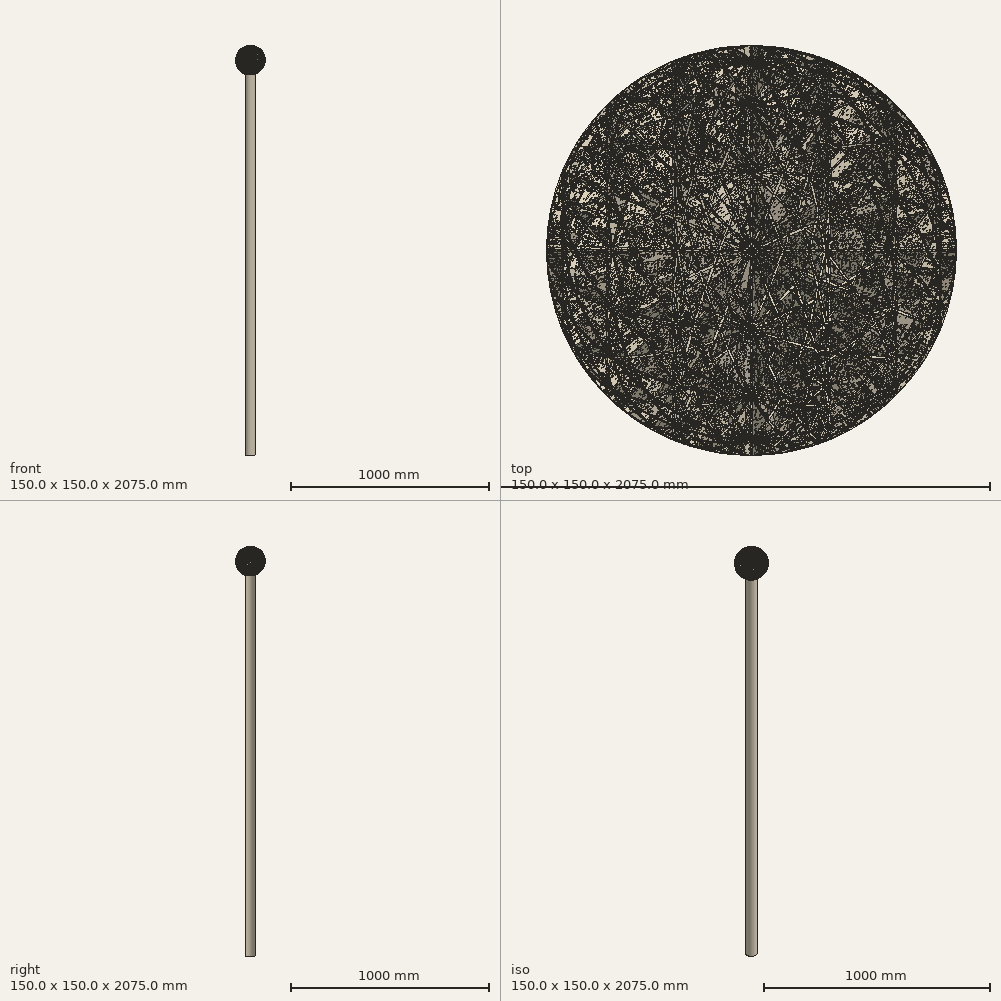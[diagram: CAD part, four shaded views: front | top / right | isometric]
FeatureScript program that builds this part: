
annotation { "Feature Type Name" : "Feature", "Feature Type Description" : "" }
export const myFeature = defineFeature(function(context is Context, id is Id, definition is map)
    precondition{}
    {
        {
            var Q0;
            Q0=qCreatedBy(makeId("Front.planeOp"),FACE);
            var sketch = newSketch(context, id + "F0", { "sketchPlane" : qUnion([Q0])});
            skCircle(sketch, "E0", {"center": v(0, 0) * mm, "radius": 75 * mm});
            skLineSegment(sketch, "E1", {"start": v(0, 0) * mm, "end": v(0, 98.01) * mm});
            skSolve(sketch);
        }
        {
            var Q0;
            Q0=qCreatedBy(makeId("Right.planeOp"),FACE);
            var sketch = newSketch(context, id + "F1", { "sketchPlane" : qUnion([Q0])});
            skCircle(sketch, "E2", {"center": v(0, 0) * mm, "radius": 75 * mm});
            skLineSegment(sketch, "E3", {"start": v(0, 0) * mm, "end": v(-91.52, 0) * mm});
            skSolve(sketch);
        }
        {
            var Q0;
            Q0=qCreatedBy(makeId("Top.planeOp"),FACE);
            var sketch = newSketch(context, id + "F2", { "sketchPlane" : qUnion([Q0])});
            skCircle(sketch, "E4", {"center": v(0, 0) * mm, "radius": 75 * mm});
            skLineSegment(sketch, "E5", {"start": v(0, 0) * mm, "end": v(107.76, 0) * mm});
            skSolve(sketch);
        }
        {
            var Q0;
            Q0=qCreatedBy(makeId("Top.planeOp"),FACE);
            var sketch = newSketch(context, id + "F3", { "sketchPlane" : qUnion([Q0])});
            skCircle(sketch, "E6", {"center": v(0, 0) * mm, "radius": 25 * mm});
            skSolve(sketch);
        }
        {
            var Q0;
            Q0=qSketchRegion(id+"F0",true);
            extrude(context, id + "F4", {"entities" : qUnion([Q0]), "endBound" : BoundingType.SYMMETRIC, "depth" : 1 * mm, "offsetDistance" : 25 * mm});
        }
        {
            var Q0;
            Q0=qSketchRegion(id+"F1",true);
            extrude(context, id + "F5", {"entities" : qUnion([Q0]), "operationType" : NewBodyOperationType.ADD, "endBound" : BoundingType.SYMMETRIC, "depth" : 1 * mm, "offsetDistance" : 25 * mm});
        }
        {
            var Q0;
            Q0=qSketchRegion(id+"F2",true);
            extrude(context, id + "F6", {"entities" : qUnion([Q0]), "operationType" : NewBodyOperationType.ADD, "endBound" : BoundingType.SYMMETRIC, "depth" : 1 * mm, "offsetDistance" : 25 * mm});
        }
        {
            var Q0;
            Q0 = qSketchRegion(id + "F3", true);
            extrude(context, id + "F7", {"entities" : qUnion([Q0]), "oppositeDirection" : true, "depth" : 2000 * mm, "offsetDistance" : 25 * mm});
        }
        {
            var Q0;
            Q0=makeQuery(id+"F4.opExtrude","SWEPT_BODY",BODY,{"disambiguationData":[OSD([sQuery(id+"F0.wireOp",EDGE,"E0")])]});
            var Q1;
            Q1=sQuery(id+"F0.wireOp",EDGE,"E1");
            var Q2;
            Q2=makeQuery(id+"F4.opExtrude","SWEPT_BODY",BODY,{"disambiguationData":[OSD([sQuery(id+"F0.wireOp",EDGE,"E0")])]});
            circularPattern(context, id + "F8", {"entities" : qUnion([Q0]), "axis" : qUnion([Q1]), "angle" : 360 * degree, "instanceCount" : 16, "equalSpace" : true});
        }
        {
            var Q0;
            Q0=makeQuery(id+"F4.opExtrude","SWEPT_BODY",BODY,{"disambiguationData":[OSD([sQuery(id+"F0.wireOp",EDGE,"E0")])]});
            var Q1;
            Q1=makeQuery(id+"F8.opPattern","COPY",BODY,{"derivedFrom":makeQuery(id+"F4.opExtrude","SWEPT_BODY",BODY,{"disambiguationData":[OSD([sQuery(id+"F0.wireOp",EDGE,"E0")])]}),"instanceName":"3"});
            var Q2;
            Q2=makeQuery(id+"F8.opPattern","COPY",BODY,{"derivedFrom":makeQuery(id+"F4.opExtrude","SWEPT_BODY",BODY,{"disambiguationData":[OSD([sQuery(id+"F0.wireOp",EDGE,"E0")])]}),"instanceName":"2"});
            var Q3;
            Q3=makeQuery(id+"F8.opPattern","COPY",BODY,{"derivedFrom":makeQuery(id+"F4.opExtrude","SWEPT_BODY",BODY,{"disambiguationData":[OSD([sQuery(id+"F0.wireOp",EDGE,"E0")])]}),"instanceName":"1"});
            var Q4;
            Q4=makeQuery(id+"F9.opPattern","COPY",BODY,{"derivedFrom":makeQuery(id+"F8.opPattern","COPY",BODY,{"derivedFrom":makeQuery(id+"F4.opExtrude","SWEPT_BODY",BODY,{"disambiguationData":[OSD([sQuery(id+"F0.wireOp",EDGE,"E0")])]}),"instanceName":"2"}),"instanceName":"1"});
            var Q5;
            Q5=makeQuery(id+"F9.opPattern","COPY",BODY,{"derivedFrom":makeQuery(id+"F8.opPattern","COPY",BODY,{"derivedFrom":makeQuery(id+"F4.opExtrude","SWEPT_BODY",BODY,{"disambiguationData":[OSD([sQuery(id+"F0.wireOp",EDGE,"E0")])]}),"instanceName":"1"}),"instanceName":"1"});
            var Q6;
            Q6=makeQuery(id+"F9.opPattern","COPY",BODY,{"derivedFrom":makeQuery(id+"F4.opExtrude","SWEPT_BODY",BODY,{"disambiguationData":[OSD([sQuery(id+"F0.wireOp",EDGE,"E0")])]}),"instanceName":"1"});
            var Q7;
            Q7=makeQuery(id+"F9.opPattern","COPY",BODY,{"derivedFrom":makeQuery(id+"F8.opPattern","COPY",BODY,{"derivedFrom":makeQuery(id+"F4.opExtrude","SWEPT_BODY",BODY,{"disambiguationData":[OSD([sQuery(id+"F0.wireOp",EDGE,"E0")])]}),"instanceName":"1"}),"instanceName":"8"});
            var Q8;
            Q8=makeQuery(id+"F9.opPattern","COPY",BODY,{"derivedFrom":makeQuery(id+"F8.opPattern","COPY",BODY,{"derivedFrom":makeQuery(id+"F4.opExtrude","SWEPT_BODY",BODY,{"disambiguationData":[OSD([sQuery(id+"F0.wireOp",EDGE,"E0")])]}),"instanceName":"15"}),"instanceName":"7"});
            var Q9;
            Q9=makeQuery(id+"F9.opPattern","COPY",BODY,{"derivedFrom":makeQuery(id+"F8.opPattern","COPY",BODY,{"derivedFrom":makeQuery(id+"F4.opExtrude","SWEPT_BODY",BODY,{"disambiguationData":[OSD([sQuery(id+"F0.wireOp",EDGE,"E0")])]}),"instanceName":"14"}),"instanceName":"7"});
            var Q10;
            Q10=makeQuery(id+"F9.opPattern","COPY",BODY,{"derivedFrom":makeQuery(id+"F8.opPattern","COPY",BODY,{"derivedFrom":makeQuery(id+"F4.opExtrude","SWEPT_BODY",BODY,{"disambiguationData":[OSD([sQuery(id+"F0.wireOp",EDGE,"E0")])]}),"instanceName":"13"}),"instanceName":"7"});
            var Q11;
            Q11=makeQuery(id+"F9.opPattern","COPY",BODY,{"derivedFrom":makeQuery(id+"F8.opPattern","COPY",BODY,{"derivedFrom":makeQuery(id+"F4.opExtrude","SWEPT_BODY",BODY,{"disambiguationData":[OSD([sQuery(id+"F0.wireOp",EDGE,"E0")])]}),"instanceName":"11"}),"instanceName":"7"});
            var Q12;
            Q12=makeQuery(id+"F9.opPattern","COPY",BODY,{"derivedFrom":makeQuery(id+"F8.opPattern","COPY",BODY,{"derivedFrom":makeQuery(id+"F4.opExtrude","SWEPT_BODY",BODY,{"disambiguationData":[OSD([sQuery(id+"F0.wireOp",EDGE,"E0")])]}),"instanceName":"10"}),"instanceName":"7"});
            var Q13;
            Q13=makeQuery(id+"F9.opPattern","COPY",BODY,{"derivedFrom":makeQuery(id+"F8.opPattern","COPY",BODY,{"derivedFrom":makeQuery(id+"F4.opExtrude","SWEPT_BODY",BODY,{"disambiguationData":[OSD([sQuery(id+"F0.wireOp",EDGE,"E0")])]}),"instanceName":"9"}),"instanceName":"7"});
            var Q14;
            Q14=makeQuery(id+"F9.opPattern","COPY",BODY,{"derivedFrom":makeQuery(id+"F8.opPattern","COPY",BODY,{"derivedFrom":makeQuery(id+"F4.opExtrude","SWEPT_BODY",BODY,{"disambiguationData":[OSD([sQuery(id+"F0.wireOp",EDGE,"E0")])]}),"instanceName":"7"}),"instanceName":"7"});
            var Q15;
            Q15=makeQuery(id+"F9.opPattern","COPY",BODY,{"derivedFrom":makeQuery(id+"F8.opPattern","COPY",BODY,{"derivedFrom":makeQuery(id+"F4.opExtrude","SWEPT_BODY",BODY,{"disambiguationData":[OSD([sQuery(id+"F0.wireOp",EDGE,"E0")])]}),"instanceName":"6"}),"instanceName":"7"});
            var Q16;
            Q16=makeQuery(id+"F9.opPattern","COPY",BODY,{"derivedFrom":makeQuery(id+"F8.opPattern","COPY",BODY,{"derivedFrom":makeQuery(id+"F4.opExtrude","SWEPT_BODY",BODY,{"disambiguationData":[OSD([sQuery(id+"F0.wireOp",EDGE,"E0")])]}),"instanceName":"5"}),"instanceName":"7"});
            var Q17;
            Q17=makeQuery(id+"F9.opPattern","COPY",BODY,{"derivedFrom":makeQuery(id+"F8.opPattern","COPY",BODY,{"derivedFrom":makeQuery(id+"F4.opExtrude","SWEPT_BODY",BODY,{"disambiguationData":[OSD([sQuery(id+"F0.wireOp",EDGE,"E0")])]}),"instanceName":"4"}),"instanceName":"7"});
            var Q18;
            Q18=makeQuery(id+"F9.opPattern","COPY",BODY,{"derivedFrom":makeQuery(id+"F8.opPattern","COPY",BODY,{"derivedFrom":makeQuery(id+"F4.opExtrude","SWEPT_BODY",BODY,{"disambiguationData":[OSD([sQuery(id+"F0.wireOp",EDGE,"E0")])]}),"instanceName":"3"}),"instanceName":"7"});
            var Q19;
            Q19=makeQuery(id+"F9.opPattern","COPY",BODY,{"derivedFrom":makeQuery(id+"F8.opPattern","COPY",BODY,{"derivedFrom":makeQuery(id+"F4.opExtrude","SWEPT_BODY",BODY,{"disambiguationData":[OSD([sQuery(id+"F0.wireOp",EDGE,"E0")])]}),"instanceName":"2"}),"instanceName":"7"});
            var Q20;
            Q20=makeQuery(id+"F9.opPattern","COPY",BODY,{"derivedFrom":makeQuery(id+"F8.opPattern","COPY",BODY,{"derivedFrom":makeQuery(id+"F4.opExtrude","SWEPT_BODY",BODY,{"disambiguationData":[OSD([sQuery(id+"F0.wireOp",EDGE,"E0")])]}),"instanceName":"1"}),"instanceName":"7"});
            var Q21;
            Q21=makeQuery(id+"F9.opPattern","COPY",BODY,{"derivedFrom":makeQuery(id+"F8.opPattern","COPY",BODY,{"derivedFrom":makeQuery(id+"F4.opExtrude","SWEPT_BODY",BODY,{"disambiguationData":[OSD([sQuery(id+"F0.wireOp",EDGE,"E0")])]}),"instanceName":"15"}),"instanceName":"6"});
            var Q22;
            Q22=makeQuery(id+"F9.opPattern","COPY",BODY,{"derivedFrom":makeQuery(id+"F8.opPattern","COPY",BODY,{"derivedFrom":makeQuery(id+"F4.opExtrude","SWEPT_BODY",BODY,{"disambiguationData":[OSD([sQuery(id+"F0.wireOp",EDGE,"E0")])]}),"instanceName":"13"}),"instanceName":"6"});
            var Q23;
            Q23=makeQuery(id+"F9.opPattern","COPY",BODY,{"derivedFrom":makeQuery(id+"F8.opPattern","COPY",BODY,{"derivedFrom":makeQuery(id+"F4.opExtrude","SWEPT_BODY",BODY,{"disambiguationData":[OSD([sQuery(id+"F0.wireOp",EDGE,"E0")])]}),"instanceName":"11"}),"instanceName":"6"});
            var Q24;
            Q24=makeQuery(id+"F9.opPattern","COPY",BODY,{"derivedFrom":makeQuery(id+"F8.opPattern","COPY",BODY,{"derivedFrom":makeQuery(id+"F4.opExtrude","SWEPT_BODY",BODY,{"disambiguationData":[OSD([sQuery(id+"F0.wireOp",EDGE,"E0")])]}),"instanceName":"10"}),"instanceName":"6"});
            var Q25;
            Q25=makeQuery(id+"F9.opPattern","COPY",BODY,{"derivedFrom":makeQuery(id+"F8.opPattern","COPY",BODY,{"derivedFrom":makeQuery(id+"F4.opExtrude","SWEPT_BODY",BODY,{"disambiguationData":[OSD([sQuery(id+"F0.wireOp",EDGE,"E0")])]}),"instanceName":"9"}),"instanceName":"6"});
            var Q26;
            Q26=makeQuery(id+"F9.opPattern","COPY",BODY,{"derivedFrom":makeQuery(id+"F8.opPattern","COPY",BODY,{"derivedFrom":makeQuery(id+"F4.opExtrude","SWEPT_BODY",BODY,{"disambiguationData":[OSD([sQuery(id+"F0.wireOp",EDGE,"E0")])]}),"instanceName":"7"}),"instanceName":"6"});
            var Q27;
            Q27=makeQuery(id+"F9.opPattern","COPY",BODY,{"derivedFrom":makeQuery(id+"F8.opPattern","COPY",BODY,{"derivedFrom":makeQuery(id+"F4.opExtrude","SWEPT_BODY",BODY,{"disambiguationData":[OSD([sQuery(id+"F0.wireOp",EDGE,"E0")])]}),"instanceName":"6"}),"instanceName":"6"});
            var Q28;
            Q28=makeQuery(id+"F9.opPattern","COPY",BODY,{"derivedFrom":makeQuery(id+"F8.opPattern","COPY",BODY,{"derivedFrom":makeQuery(id+"F4.opExtrude","SWEPT_BODY",BODY,{"disambiguationData":[OSD([sQuery(id+"F0.wireOp",EDGE,"E0")])]}),"instanceName":"5"}),"instanceName":"6"});
            var Q29;
            Q29=makeQuery(id+"F9.opPattern","COPY",BODY,{"derivedFrom":makeQuery(id+"F8.opPattern","COPY",BODY,{"derivedFrom":makeQuery(id+"F4.opExtrude","SWEPT_BODY",BODY,{"disambiguationData":[OSD([sQuery(id+"F0.wireOp",EDGE,"E0")])]}),"instanceName":"3"}),"instanceName":"6"});
            var Q30;
            Q30=makeQuery(id+"F9.opPattern","COPY",BODY,{"derivedFrom":makeQuery(id+"F8.opPattern","COPY",BODY,{"derivedFrom":makeQuery(id+"F4.opExtrude","SWEPT_BODY",BODY,{"disambiguationData":[OSD([sQuery(id+"F0.wireOp",EDGE,"E0")])]}),"instanceName":"2"}),"instanceName":"6"});
            var Q31;
            Q31=makeQuery(id+"F9.opPattern","COPY",BODY,{"derivedFrom":makeQuery(id+"F8.opPattern","COPY",BODY,{"derivedFrom":makeQuery(id+"F4.opExtrude","SWEPT_BODY",BODY,{"disambiguationData":[OSD([sQuery(id+"F0.wireOp",EDGE,"E0")])]}),"instanceName":"1"}),"instanceName":"6"});
            var Q32;
            Q32=makeQuery(id+"F9.opPattern","COPY",BODY,{"derivedFrom":makeQuery(id+"F4.opExtrude","SWEPT_BODY",BODY,{"disambiguationData":[OSD([sQuery(id+"F0.wireOp",EDGE,"E0")])]}),"instanceName":"6"});
            var Q33;
            Q33=makeQuery(id+"F9.opPattern","COPY",BODY,{"derivedFrom":makeQuery(id+"F8.opPattern","COPY",BODY,{"derivedFrom":makeQuery(id+"F4.opExtrude","SWEPT_BODY",BODY,{"disambiguationData":[OSD([sQuery(id+"F0.wireOp",EDGE,"E0")])]}),"instanceName":"14"}),"instanceName":"5"});
            var Q34;
            Q34=makeQuery(id+"F9.opPattern","COPY",BODY,{"derivedFrom":makeQuery(id+"F8.opPattern","COPY",BODY,{"derivedFrom":makeQuery(id+"F4.opExtrude","SWEPT_BODY",BODY,{"disambiguationData":[OSD([sQuery(id+"F0.wireOp",EDGE,"E0")])]}),"instanceName":"13"}),"instanceName":"5"});
            var Q35;
            Q35=makeQuery(id+"F9.opPattern","COPY",BODY,{"derivedFrom":makeQuery(id+"F8.opPattern","COPY",BODY,{"derivedFrom":makeQuery(id+"F4.opExtrude","SWEPT_BODY",BODY,{"disambiguationData":[OSD([sQuery(id+"F0.wireOp",EDGE,"E0")])]}),"instanceName":"11"}),"instanceName":"5"});
            var Q36;
            Q36=makeQuery(id+"F9.opPattern","COPY",BODY,{"derivedFrom":makeQuery(id+"F8.opPattern","COPY",BODY,{"derivedFrom":makeQuery(id+"F4.opExtrude","SWEPT_BODY",BODY,{"disambiguationData":[OSD([sQuery(id+"F0.wireOp",EDGE,"E0")])]}),"instanceName":"10"}),"instanceName":"5"});
            var Q37;
            Q37=makeQuery(id+"F9.opPattern","COPY",BODY,{"derivedFrom":makeQuery(id+"F8.opPattern","COPY",BODY,{"derivedFrom":makeQuery(id+"F4.opExtrude","SWEPT_BODY",BODY,{"disambiguationData":[OSD([sQuery(id+"F0.wireOp",EDGE,"E0")])]}),"instanceName":"9"}),"instanceName":"5"});
            var Q38;
            Q38=makeQuery(id+"F9.opPattern","COPY",BODY,{"derivedFrom":makeQuery(id+"F8.opPattern","COPY",BODY,{"derivedFrom":makeQuery(id+"F4.opExtrude","SWEPT_BODY",BODY,{"disambiguationData":[OSD([sQuery(id+"F0.wireOp",EDGE,"E0")])]}),"instanceName":"8"}),"instanceName":"5"});
            var Q39;
            Q39=makeQuery(id+"F9.opPattern","COPY",BODY,{"derivedFrom":makeQuery(id+"F8.opPattern","COPY",BODY,{"derivedFrom":makeQuery(id+"F4.opExtrude","SWEPT_BODY",BODY,{"disambiguationData":[OSD([sQuery(id+"F0.wireOp",EDGE,"E0")])]}),"instanceName":"7"}),"instanceName":"5"});
            var Q40;
            Q40=makeQuery(id+"F9.opPattern","COPY",BODY,{"derivedFrom":makeQuery(id+"F8.opPattern","COPY",BODY,{"derivedFrom":makeQuery(id+"F4.opExtrude","SWEPT_BODY",BODY,{"disambiguationData":[OSD([sQuery(id+"F0.wireOp",EDGE,"E0")])]}),"instanceName":"6"}),"instanceName":"5"});
            var Q41;
            Q41=makeQuery(id+"F9.opPattern","COPY",BODY,{"derivedFrom":makeQuery(id+"F8.opPattern","COPY",BODY,{"derivedFrom":makeQuery(id+"F4.opExtrude","SWEPT_BODY",BODY,{"disambiguationData":[OSD([sQuery(id+"F0.wireOp",EDGE,"E0")])]}),"instanceName":"5"}),"instanceName":"5"});
            var Q42;
            Q42=makeQuery(id+"F9.opPattern","COPY",BODY,{"derivedFrom":makeQuery(id+"F8.opPattern","COPY",BODY,{"derivedFrom":makeQuery(id+"F4.opExtrude","SWEPT_BODY",BODY,{"disambiguationData":[OSD([sQuery(id+"F0.wireOp",EDGE,"E0")])]}),"instanceName":"3"}),"instanceName":"5"});
            var Q43;
            Q43=makeQuery(id+"F9.opPattern","COPY",BODY,{"derivedFrom":makeQuery(id+"F8.opPattern","COPY",BODY,{"derivedFrom":makeQuery(id+"F4.opExtrude","SWEPT_BODY",BODY,{"disambiguationData":[OSD([sQuery(id+"F0.wireOp",EDGE,"E0")])]}),"instanceName":"2"}),"instanceName":"5"});
            var Q44;
            Q44=makeQuery(id+"F9.opPattern","COPY",BODY,{"derivedFrom":makeQuery(id+"F8.opPattern","COPY",BODY,{"derivedFrom":makeQuery(id+"F4.opExtrude","SWEPT_BODY",BODY,{"disambiguationData":[OSD([sQuery(id+"F0.wireOp",EDGE,"E0")])]}),"instanceName":"1"}),"instanceName":"5"});
            var Q45;
            Q45=makeQuery(id+"F9.opPattern","COPY",BODY,{"derivedFrom":makeQuery(id+"F4.opExtrude","SWEPT_BODY",BODY,{"disambiguationData":[OSD([sQuery(id+"F0.wireOp",EDGE,"E0")])]}),"instanceName":"5"});
            var Q46;
            Q46=makeQuery(id+"F9.opPattern","COPY",BODY,{"derivedFrom":makeQuery(id+"F8.opPattern","COPY",BODY,{"derivedFrom":makeQuery(id+"F4.opExtrude","SWEPT_BODY",BODY,{"disambiguationData":[OSD([sQuery(id+"F0.wireOp",EDGE,"E0")])]}),"instanceName":"13"}),"instanceName":"4"});
            var Q47;
            Q47=makeQuery(id+"F9.opPattern","COPY",BODY,{"derivedFrom":makeQuery(id+"F8.opPattern","COPY",BODY,{"derivedFrom":makeQuery(id+"F4.opExtrude","SWEPT_BODY",BODY,{"disambiguationData":[OSD([sQuery(id+"F0.wireOp",EDGE,"E0")])]}),"instanceName":"11"}),"instanceName":"4"});
            var Q48;
            Q48=makeQuery(id+"F9.opPattern","COPY",BODY,{"derivedFrom":makeQuery(id+"F8.opPattern","COPY",BODY,{"derivedFrom":makeQuery(id+"F4.opExtrude","SWEPT_BODY",BODY,{"disambiguationData":[OSD([sQuery(id+"F0.wireOp",EDGE,"E0")])]}),"instanceName":"10"}),"instanceName":"4"});
            var Q49;
            Q49=makeQuery(id+"F9.opPattern","COPY",BODY,{"derivedFrom":makeQuery(id+"F8.opPattern","COPY",BODY,{"derivedFrom":makeQuery(id+"F4.opExtrude","SWEPT_BODY",BODY,{"disambiguationData":[OSD([sQuery(id+"F0.wireOp",EDGE,"E0")])]}),"instanceName":"9"}),"instanceName":"4"});
            var Q50;
            Q50=makeQuery(id+"F9.opPattern","COPY",BODY,{"derivedFrom":makeQuery(id+"F8.opPattern","COPY",BODY,{"derivedFrom":makeQuery(id+"F4.opExtrude","SWEPT_BODY",BODY,{"disambiguationData":[OSD([sQuery(id+"F0.wireOp",EDGE,"E0")])]}),"instanceName":"7"}),"instanceName":"4"});
            var Q51;
            Q51=makeQuery(id+"F9.opPattern","COPY",BODY,{"derivedFrom":makeQuery(id+"F8.opPattern","COPY",BODY,{"derivedFrom":makeQuery(id+"F4.opExtrude","SWEPT_BODY",BODY,{"disambiguationData":[OSD([sQuery(id+"F0.wireOp",EDGE,"E0")])]}),"instanceName":"6"}),"instanceName":"4"});
            var Q52;
            Q52=makeQuery(id+"F9.opPattern","COPY",BODY,{"derivedFrom":makeQuery(id+"F8.opPattern","COPY",BODY,{"derivedFrom":makeQuery(id+"F4.opExtrude","SWEPT_BODY",BODY,{"disambiguationData":[OSD([sQuery(id+"F0.wireOp",EDGE,"E0")])]}),"instanceName":"5"}),"instanceName":"4"});
            var Q53;
            Q53=makeQuery(id+"F9.opPattern","COPY",BODY,{"derivedFrom":makeQuery(id+"F8.opPattern","COPY",BODY,{"derivedFrom":makeQuery(id+"F4.opExtrude","SWEPT_BODY",BODY,{"disambiguationData":[OSD([sQuery(id+"F0.wireOp",EDGE,"E0")])]}),"instanceName":"3"}),"instanceName":"4"});
            var Q54;
            Q54=makeQuery(id+"F9.opPattern","COPY",BODY,{"derivedFrom":makeQuery(id+"F8.opPattern","COPY",BODY,{"derivedFrom":makeQuery(id+"F4.opExtrude","SWEPT_BODY",BODY,{"disambiguationData":[OSD([sQuery(id+"F0.wireOp",EDGE,"E0")])]}),"instanceName":"2"}),"instanceName":"4"});
            var Q55;
            Q55=makeQuery(id+"F9.opPattern","COPY",BODY,{"derivedFrom":makeQuery(id+"F8.opPattern","COPY",BODY,{"derivedFrom":makeQuery(id+"F4.opExtrude","SWEPT_BODY",BODY,{"disambiguationData":[OSD([sQuery(id+"F0.wireOp",EDGE,"E0")])]}),"instanceName":"1"}),"instanceName":"4"});
            var Q56;
            Q56=makeQuery(id+"F9.opPattern","COPY",BODY,{"derivedFrom":makeQuery(id+"F8.opPattern","COPY",BODY,{"derivedFrom":makeQuery(id+"F4.opExtrude","SWEPT_BODY",BODY,{"disambiguationData":[OSD([sQuery(id+"F0.wireOp",EDGE,"E0")])]}),"instanceName":"15"}),"instanceName":"3"});
            var Q57;
            Q57=makeQuery(id+"F9.opPattern","COPY",BODY,{"derivedFrom":makeQuery(id+"F8.opPattern","COPY",BODY,{"derivedFrom":makeQuery(id+"F4.opExtrude","SWEPT_BODY",BODY,{"disambiguationData":[OSD([sQuery(id+"F0.wireOp",EDGE,"E0")])]}),"instanceName":"14"}),"instanceName":"3"});
            var Q58;
            Q58=makeQuery(id+"F9.opPattern","COPY",BODY,{"derivedFrom":makeQuery(id+"F8.opPattern","COPY",BODY,{"derivedFrom":makeQuery(id+"F4.opExtrude","SWEPT_BODY",BODY,{"disambiguationData":[OSD([sQuery(id+"F0.wireOp",EDGE,"E0")])]}),"instanceName":"13"}),"instanceName":"3"});
            var Q59;
            Q59=makeQuery(id+"F9.opPattern","COPY",BODY,{"derivedFrom":makeQuery(id+"F8.opPattern","COPY",BODY,{"derivedFrom":makeQuery(id+"F4.opExtrude","SWEPT_BODY",BODY,{"disambiguationData":[OSD([sQuery(id+"F0.wireOp",EDGE,"E0")])]}),"instanceName":"11"}),"instanceName":"3"});
            var Q60;
            Q60=makeQuery(id+"F9.opPattern","COPY",BODY,{"derivedFrom":makeQuery(id+"F8.opPattern","COPY",BODY,{"derivedFrom":makeQuery(id+"F4.opExtrude","SWEPT_BODY",BODY,{"disambiguationData":[OSD([sQuery(id+"F0.wireOp",EDGE,"E0")])]}),"instanceName":"10"}),"instanceName":"3"});
            var Q61;
            Q61=makeQuery(id+"F9.opPattern","COPY",BODY,{"derivedFrom":makeQuery(id+"F8.opPattern","COPY",BODY,{"derivedFrom":makeQuery(id+"F4.opExtrude","SWEPT_BODY",BODY,{"disambiguationData":[OSD([sQuery(id+"F0.wireOp",EDGE,"E0")])]}),"instanceName":"9"}),"instanceName":"3"});
            var Q62;
            Q62=makeQuery(id+"F9.opPattern","COPY",BODY,{"derivedFrom":makeQuery(id+"F8.opPattern","COPY",BODY,{"derivedFrom":makeQuery(id+"F4.opExtrude","SWEPT_BODY",BODY,{"disambiguationData":[OSD([sQuery(id+"F0.wireOp",EDGE,"E0")])]}),"instanceName":"8"}),"instanceName":"3"});
            var Q63;
            Q63=makeQuery(id+"F9.opPattern","COPY",BODY,{"derivedFrom":makeQuery(id+"F8.opPattern","COPY",BODY,{"derivedFrom":makeQuery(id+"F4.opExtrude","SWEPT_BODY",BODY,{"disambiguationData":[OSD([sQuery(id+"F0.wireOp",EDGE,"E0")])]}),"instanceName":"7"}),"instanceName":"3"});
            var Q64;
            Q64=makeQuery(id+"F9.opPattern","COPY",BODY,{"derivedFrom":makeQuery(id+"F8.opPattern","COPY",BODY,{"derivedFrom":makeQuery(id+"F4.opExtrude","SWEPT_BODY",BODY,{"disambiguationData":[OSD([sQuery(id+"F0.wireOp",EDGE,"E0")])]}),"instanceName":"6"}),"instanceName":"3"});
            var Q65;
            Q65=makeQuery(id+"F9.opPattern","COPY",BODY,{"derivedFrom":makeQuery(id+"F8.opPattern","COPY",BODY,{"derivedFrom":makeQuery(id+"F4.opExtrude","SWEPT_BODY",BODY,{"disambiguationData":[OSD([sQuery(id+"F0.wireOp",EDGE,"E0")])]}),"instanceName":"5"}),"instanceName":"3"});
            var Q66;
            Q66=makeQuery(id+"F9.opPattern","COPY",BODY,{"derivedFrom":makeQuery(id+"F8.opPattern","COPY",BODY,{"derivedFrom":makeQuery(id+"F4.opExtrude","SWEPT_BODY",BODY,{"disambiguationData":[OSD([sQuery(id+"F0.wireOp",EDGE,"E0")])]}),"instanceName":"4"}),"instanceName":"3"});
            var Q67;
            Q67=makeQuery(id+"F9.opPattern","COPY",BODY,{"derivedFrom":makeQuery(id+"F8.opPattern","COPY",BODY,{"derivedFrom":makeQuery(id+"F4.opExtrude","SWEPT_BODY",BODY,{"disambiguationData":[OSD([sQuery(id+"F0.wireOp",EDGE,"E0")])]}),"instanceName":"3"}),"instanceName":"3"});
            var Q68;
            Q68=makeQuery(id+"F9.opPattern","COPY",BODY,{"derivedFrom":makeQuery(id+"F8.opPattern","COPY",BODY,{"derivedFrom":makeQuery(id+"F4.opExtrude","SWEPT_BODY",BODY,{"disambiguationData":[OSD([sQuery(id+"F0.wireOp",EDGE,"E0")])]}),"instanceName":"2"}),"instanceName":"3"});
            var Q69;
            Q69=makeQuery(id+"F9.opPattern","COPY",BODY,{"derivedFrom":makeQuery(id+"F8.opPattern","COPY",BODY,{"derivedFrom":makeQuery(id+"F4.opExtrude","SWEPT_BODY",BODY,{"disambiguationData":[OSD([sQuery(id+"F0.wireOp",EDGE,"E0")])]}),"instanceName":"1"}),"instanceName":"3"});
            var Q70;
            Q70=makeQuery(id+"F9.opPattern","COPY",BODY,{"derivedFrom":makeQuery(id+"F4.opExtrude","SWEPT_BODY",BODY,{"disambiguationData":[OSD([sQuery(id+"F0.wireOp",EDGE,"E0")])]}),"instanceName":"3"});
            var Q71;
            Q71=makeQuery(id+"F9.opPattern","COPY",BODY,{"derivedFrom":makeQuery(id+"F8.opPattern","COPY",BODY,{"derivedFrom":makeQuery(id+"F4.opExtrude","SWEPT_BODY",BODY,{"disambiguationData":[OSD([sQuery(id+"F0.wireOp",EDGE,"E0")])]}),"instanceName":"14"}),"instanceName":"2"});
            var Q72;
            Q72=makeQuery(id+"F9.opPattern","COPY",BODY,{"derivedFrom":makeQuery(id+"F8.opPattern","COPY",BODY,{"derivedFrom":makeQuery(id+"F4.opExtrude","SWEPT_BODY",BODY,{"disambiguationData":[OSD([sQuery(id+"F0.wireOp",EDGE,"E0")])]}),"instanceName":"13"}),"instanceName":"2"});
            var Q73;
            Q73=makeQuery(id+"F9.opPattern","COPY",BODY,{"derivedFrom":makeQuery(id+"F8.opPattern","COPY",BODY,{"derivedFrom":makeQuery(id+"F4.opExtrude","SWEPT_BODY",BODY,{"disambiguationData":[OSD([sQuery(id+"F0.wireOp",EDGE,"E0")])]}),"instanceName":"12"}),"instanceName":"2"});
            var Q74;
            Q74=makeQuery(id+"F9.opPattern","COPY",BODY,{"derivedFrom":makeQuery(id+"F8.opPattern","COPY",BODY,{"derivedFrom":makeQuery(id+"F4.opExtrude","SWEPT_BODY",BODY,{"disambiguationData":[OSD([sQuery(id+"F0.wireOp",EDGE,"E0")])]}),"instanceName":"11"}),"instanceName":"2"});
            var Q75;
            Q75=makeQuery(id+"F9.opPattern","COPY",BODY,{"derivedFrom":makeQuery(id+"F8.opPattern","COPY",BODY,{"derivedFrom":makeQuery(id+"F4.opExtrude","SWEPT_BODY",BODY,{"disambiguationData":[OSD([sQuery(id+"F0.wireOp",EDGE,"E0")])]}),"instanceName":"10"}),"instanceName":"2"});
            var Q76;
            Q76=makeQuery(id+"F9.opPattern","COPY",BODY,{"derivedFrom":makeQuery(id+"F8.opPattern","COPY",BODY,{"derivedFrom":makeQuery(id+"F4.opExtrude","SWEPT_BODY",BODY,{"disambiguationData":[OSD([sQuery(id+"F0.wireOp",EDGE,"E0")])]}),"instanceName":"9"}),"instanceName":"2"});
            var Q77;
            Q77=makeQuery(id+"F9.opPattern","COPY",BODY,{"derivedFrom":makeQuery(id+"F8.opPattern","COPY",BODY,{"derivedFrom":makeQuery(id+"F4.opExtrude","SWEPT_BODY",BODY,{"disambiguationData":[OSD([sQuery(id+"F0.wireOp",EDGE,"E0")])]}),"instanceName":"8"}),"instanceName":"2"});
            var Q78;
            Q78=makeQuery(id+"F9.opPattern","COPY",BODY,{"derivedFrom":makeQuery(id+"F8.opPattern","COPY",BODY,{"derivedFrom":makeQuery(id+"F4.opExtrude","SWEPT_BODY",BODY,{"disambiguationData":[OSD([sQuery(id+"F0.wireOp",EDGE,"E0")])]}),"instanceName":"7"}),"instanceName":"2"});
            var Q79;
            Q79=makeQuery(id+"F9.opPattern","COPY",BODY,{"derivedFrom":makeQuery(id+"F8.opPattern","COPY",BODY,{"derivedFrom":makeQuery(id+"F4.opExtrude","SWEPT_BODY",BODY,{"disambiguationData":[OSD([sQuery(id+"F0.wireOp",EDGE,"E0")])]}),"instanceName":"6"}),"instanceName":"2"});
            var Q80;
            Q80=makeQuery(id+"F9.opPattern","COPY",BODY,{"derivedFrom":makeQuery(id+"F8.opPattern","COPY",BODY,{"derivedFrom":makeQuery(id+"F4.opExtrude","SWEPT_BODY",BODY,{"disambiguationData":[OSD([sQuery(id+"F0.wireOp",EDGE,"E0")])]}),"instanceName":"5"}),"instanceName":"2"});
            var Q81;
            Q81=makeQuery(id+"F9.opPattern","COPY",BODY,{"derivedFrom":makeQuery(id+"F8.opPattern","COPY",BODY,{"derivedFrom":makeQuery(id+"F4.opExtrude","SWEPT_BODY",BODY,{"disambiguationData":[OSD([sQuery(id+"F0.wireOp",EDGE,"E0")])]}),"instanceName":"4"}),"instanceName":"2"});
            var Q82;
            Q82=makeQuery(id+"F9.opPattern","COPY",BODY,{"derivedFrom":makeQuery(id+"F8.opPattern","COPY",BODY,{"derivedFrom":makeQuery(id+"F4.opExtrude","SWEPT_BODY",BODY,{"disambiguationData":[OSD([sQuery(id+"F0.wireOp",EDGE,"E0")])]}),"instanceName":"3"}),"instanceName":"2"});
            var Q83;
            Q83=makeQuery(id+"F9.opPattern","COPY",BODY,{"derivedFrom":makeQuery(id+"F8.opPattern","COPY",BODY,{"derivedFrom":makeQuery(id+"F4.opExtrude","SWEPT_BODY",BODY,{"disambiguationData":[OSD([sQuery(id+"F0.wireOp",EDGE,"E0")])]}),"instanceName":"2"}),"instanceName":"2"});
            var Q84;
            Q84=makeQuery(id+"F9.opPattern","COPY",BODY,{"derivedFrom":makeQuery(id+"F8.opPattern","COPY",BODY,{"derivedFrom":makeQuery(id+"F4.opExtrude","SWEPT_BODY",BODY,{"disambiguationData":[OSD([sQuery(id+"F0.wireOp",EDGE,"E0")])]}),"instanceName":"1"}),"instanceName":"2"});
            var Q85;
            Q85=makeQuery(id+"F9.opPattern","COPY",BODY,{"derivedFrom":makeQuery(id+"F4.opExtrude","SWEPT_BODY",BODY,{"disambiguationData":[OSD([sQuery(id+"F0.wireOp",EDGE,"E0")])]}),"instanceName":"2"});
            var Q86;
            Q86=makeQuery(id+"F9.opPattern","COPY",BODY,{"derivedFrom":makeQuery(id+"F8.opPattern","COPY",BODY,{"derivedFrom":makeQuery(id+"F4.opExtrude","SWEPT_BODY",BODY,{"disambiguationData":[OSD([sQuery(id+"F0.wireOp",EDGE,"E0")])]}),"instanceName":"15"}),"instanceName":"1"});
            var Q87;
            Q87=makeQuery(id+"F9.opPattern","COPY",BODY,{"derivedFrom":makeQuery(id+"F8.opPattern","COPY",BODY,{"derivedFrom":makeQuery(id+"F4.opExtrude","SWEPT_BODY",BODY,{"disambiguationData":[OSD([sQuery(id+"F0.wireOp",EDGE,"E0")])]}),"instanceName":"14"}),"instanceName":"1"});
            var Q88;
            Q88=makeQuery(id+"F9.opPattern","COPY",BODY,{"derivedFrom":makeQuery(id+"F8.opPattern","COPY",BODY,{"derivedFrom":makeQuery(id+"F4.opExtrude","SWEPT_BODY",BODY,{"disambiguationData":[OSD([sQuery(id+"F0.wireOp",EDGE,"E0")])]}),"instanceName":"12"}),"instanceName":"1"});
            var Q89;
            Q89=makeQuery(id+"F9.opPattern","COPY",BODY,{"derivedFrom":makeQuery(id+"F8.opPattern","COPY",BODY,{"derivedFrom":makeQuery(id+"F4.opExtrude","SWEPT_BODY",BODY,{"disambiguationData":[OSD([sQuery(id+"F0.wireOp",EDGE,"E0")])]}),"instanceName":"11"}),"instanceName":"1"});
            var Q90;
            Q90=makeQuery(id+"F9.opPattern","COPY",BODY,{"derivedFrom":makeQuery(id+"F8.opPattern","COPY",BODY,{"derivedFrom":makeQuery(id+"F4.opExtrude","SWEPT_BODY",BODY,{"disambiguationData":[OSD([sQuery(id+"F0.wireOp",EDGE,"E0")])]}),"instanceName":"10"}),"instanceName":"1"});
            var Q91;
            Q91=makeQuery(id+"F9.opPattern","COPY",BODY,{"derivedFrom":makeQuery(id+"F8.opPattern","COPY",BODY,{"derivedFrom":makeQuery(id+"F4.opExtrude","SWEPT_BODY",BODY,{"disambiguationData":[OSD([sQuery(id+"F0.wireOp",EDGE,"E0")])]}),"instanceName":"9"}),"instanceName":"1"});
            var Q92;
            Q92=makeQuery(id+"F9.opPattern","COPY",BODY,{"derivedFrom":makeQuery(id+"F8.opPattern","COPY",BODY,{"derivedFrom":makeQuery(id+"F4.opExtrude","SWEPT_BODY",BODY,{"disambiguationData":[OSD([sQuery(id+"F0.wireOp",EDGE,"E0")])]}),"instanceName":"8"}),"instanceName":"1"});
            var Q93;
            Q93=makeQuery(id+"F9.opPattern","COPY",BODY,{"derivedFrom":makeQuery(id+"F8.opPattern","COPY",BODY,{"derivedFrom":makeQuery(id+"F4.opExtrude","SWEPT_BODY",BODY,{"disambiguationData":[OSD([sQuery(id+"F0.wireOp",EDGE,"E0")])]}),"instanceName":"7"}),"instanceName":"1"});
            var Q94;
            Q94=makeQuery(id+"F9.opPattern","COPY",BODY,{"derivedFrom":makeQuery(id+"F8.opPattern","COPY",BODY,{"derivedFrom":makeQuery(id+"F4.opExtrude","SWEPT_BODY",BODY,{"disambiguationData":[OSD([sQuery(id+"F0.wireOp",EDGE,"E0")])]}),"instanceName":"6"}),"instanceName":"1"});
            var Q95;
            Q95=makeQuery(id+"F9.opPattern","COPY",BODY,{"derivedFrom":makeQuery(id+"F8.opPattern","COPY",BODY,{"derivedFrom":makeQuery(id+"F4.opExtrude","SWEPT_BODY",BODY,{"disambiguationData":[OSD([sQuery(id+"F0.wireOp",EDGE,"E0")])]}),"instanceName":"5"}),"instanceName":"1"});
            var Q96;
            Q96=makeQuery(id+"F9.opPattern","COPY",BODY,{"derivedFrom":makeQuery(id+"F8.opPattern","COPY",BODY,{"derivedFrom":makeQuery(id+"F4.opExtrude","SWEPT_BODY",BODY,{"disambiguationData":[OSD([sQuery(id+"F0.wireOp",EDGE,"E0")])]}),"instanceName":"4"}),"instanceName":"1"});
            var Q97;
            Q97=makeQuery(id+"F9.opPattern","COPY",BODY,{"derivedFrom":makeQuery(id+"F8.opPattern","COPY",BODY,{"derivedFrom":makeQuery(id+"F4.opExtrude","SWEPT_BODY",BODY,{"disambiguationData":[OSD([sQuery(id+"F0.wireOp",EDGE,"E0")])]}),"instanceName":"3"}),"instanceName":"1"});
            var Q98;
            Q98=makeQuery(id+"F8.opPattern","COPY",BODY,{"derivedFrom":makeQuery(id+"F4.opExtrude","SWEPT_BODY",BODY,{"disambiguationData":[OSD([sQuery(id+"F0.wireOp",EDGE,"E0")])]}),"instanceName":"15"});
            var Q99;
            Q99=makeQuery(id+"F8.opPattern","COPY",BODY,{"derivedFrom":makeQuery(id+"F4.opExtrude","SWEPT_BODY",BODY,{"disambiguationData":[OSD([sQuery(id+"F0.wireOp",EDGE,"E0")])]}),"instanceName":"13"});
            var Q100;
            Q100=makeQuery(id+"F8.opPattern","COPY",BODY,{"derivedFrom":makeQuery(id+"F4.opExtrude","SWEPT_BODY",BODY,{"disambiguationData":[OSD([sQuery(id+"F0.wireOp",EDGE,"E0")])]}),"instanceName":"11"});
            var Q101;
            Q101=makeQuery(id+"F8.opPattern","COPY",BODY,{"derivedFrom":makeQuery(id+"F4.opExtrude","SWEPT_BODY",BODY,{"disambiguationData":[OSD([sQuery(id+"F0.wireOp",EDGE,"E0")])]}),"instanceName":"10"});
            var Q102;
            Q102=makeQuery(id+"F8.opPattern","COPY",BODY,{"derivedFrom":makeQuery(id+"F4.opExtrude","SWEPT_BODY",BODY,{"disambiguationData":[OSD([sQuery(id+"F0.wireOp",EDGE,"E0")])]}),"instanceName":"9"});
            var Q103;
            Q103=makeQuery(id+"F8.opPattern","COPY",BODY,{"derivedFrom":makeQuery(id+"F4.opExtrude","SWEPT_BODY",BODY,{"disambiguationData":[OSD([sQuery(id+"F0.wireOp",EDGE,"E0")])]}),"instanceName":"5"});
            var Q104;
            Q104=makeQuery(id+"F8.opPattern","COPY",BODY,{"derivedFrom":makeQuery(id+"F4.opExtrude","SWEPT_BODY",BODY,{"disambiguationData":[OSD([sQuery(id+"F0.wireOp",EDGE,"E0")])]}),"instanceName":"6"});
            var Q105;
            Q105=makeQuery(id+"F8.opPattern","COPY",BODY,{"derivedFrom":makeQuery(id+"F4.opExtrude","SWEPT_BODY",BODY,{"disambiguationData":[OSD([sQuery(id+"F0.wireOp",EDGE,"E0")])]}),"instanceName":"7"});
            var Q106;
            Q106=makeQuery(id+"F9.opPattern","COPY",BODY,{"derivedFrom":makeQuery(id+"F8.opPattern","COPY",BODY,{"derivedFrom":makeQuery(id+"F4.opExtrude","SWEPT_BODY",BODY,{"disambiguationData":[OSD([sQuery(id+"F0.wireOp",EDGE,"E0")])]}),"instanceName":"2"}),"instanceName":"8"});
            var Q107;
            Q107=makeQuery(id+"F9.opPattern","COPY",BODY,{"derivedFrom":makeQuery(id+"F8.opPattern","COPY",BODY,{"derivedFrom":makeQuery(id+"F4.opExtrude","SWEPT_BODY",BODY,{"disambiguationData":[OSD([sQuery(id+"F0.wireOp",EDGE,"E0")])]}),"instanceName":"3"}),"instanceName":"8"});
            var Q108;
            Q108=makeQuery(id+"F9.opPattern","COPY",BODY,{"derivedFrom":makeQuery(id+"F8.opPattern","COPY",BODY,{"derivedFrom":makeQuery(id+"F4.opExtrude","SWEPT_BODY",BODY,{"disambiguationData":[OSD([sQuery(id+"F0.wireOp",EDGE,"E0")])]}),"instanceName":"6"}),"instanceName":"8"});
            var Q109;
            Q109=makeQuery(id+"F9.opPattern","COPY",BODY,{"derivedFrom":makeQuery(id+"F8.opPattern","COPY",BODY,{"derivedFrom":makeQuery(id+"F4.opExtrude","SWEPT_BODY",BODY,{"disambiguationData":[OSD([sQuery(id+"F0.wireOp",EDGE,"E0")])]}),"instanceName":"10"}),"instanceName":"8"});
            var Q110;
            Q110=makeQuery(id+"F9.opPattern","COPY",BODY,{"derivedFrom":makeQuery(id+"F8.opPattern","COPY",BODY,{"derivedFrom":makeQuery(id+"F4.opExtrude","SWEPT_BODY",BODY,{"disambiguationData":[OSD([sQuery(id+"F0.wireOp",EDGE,"E0")])]}),"instanceName":"1"}),"instanceName":"9"});
            var Q111;
            Q111=makeQuery(id+"F9.opPattern","COPY",BODY,{"derivedFrom":makeQuery(id+"F8.opPattern","COPY",BODY,{"derivedFrom":makeQuery(id+"F4.opExtrude","SWEPT_BODY",BODY,{"disambiguationData":[OSD([sQuery(id+"F0.wireOp",EDGE,"E0")])]}),"instanceName":"2"}),"instanceName":"9"});
            var Q112;
            Q112=makeQuery(id+"F9.opPattern","COPY",BODY,{"derivedFrom":makeQuery(id+"F8.opPattern","COPY",BODY,{"derivedFrom":makeQuery(id+"F4.opExtrude","SWEPT_BODY",BODY,{"disambiguationData":[OSD([sQuery(id+"F0.wireOp",EDGE,"E0")])]}),"instanceName":"3"}),"instanceName":"9"});
            var Q113;
            Q113=makeQuery(id+"F9.opPattern","COPY",BODY,{"derivedFrom":makeQuery(id+"F8.opPattern","COPY",BODY,{"derivedFrom":makeQuery(id+"F4.opExtrude","SWEPT_BODY",BODY,{"disambiguationData":[OSD([sQuery(id+"F0.wireOp",EDGE,"E0")])]}),"instanceName":"4"}),"instanceName":"9"});
            var Q114;
            Q114=makeQuery(id+"F9.opPattern","COPY",BODY,{"derivedFrom":makeQuery(id+"F8.opPattern","COPY",BODY,{"derivedFrom":makeQuery(id+"F4.opExtrude","SWEPT_BODY",BODY,{"disambiguationData":[OSD([sQuery(id+"F0.wireOp",EDGE,"E0")])]}),"instanceName":"6"}),"instanceName":"9"});
            var Q115;
            Q115=makeQuery(id+"F9.opPattern","COPY",BODY,{"derivedFrom":makeQuery(id+"F8.opPattern","COPY",BODY,{"derivedFrom":makeQuery(id+"F4.opExtrude","SWEPT_BODY",BODY,{"disambiguationData":[OSD([sQuery(id+"F0.wireOp",EDGE,"E0")])]}),"instanceName":"7"}),"instanceName":"9"});
            var Q116;
            Q116=makeQuery(id+"F9.opPattern","COPY",BODY,{"derivedFrom":makeQuery(id+"F8.opPattern","COPY",BODY,{"derivedFrom":makeQuery(id+"F4.opExtrude","SWEPT_BODY",BODY,{"disambiguationData":[OSD([sQuery(id+"F0.wireOp",EDGE,"E0")])]}),"instanceName":"14"}),"instanceName":"9"});
            var Q117;
            Q117=makeQuery(id+"F9.opPattern","COPY",BODY,{"derivedFrom":makeQuery(id+"F8.opPattern","COPY",BODY,{"derivedFrom":makeQuery(id+"F4.opExtrude","SWEPT_BODY",BODY,{"disambiguationData":[OSD([sQuery(id+"F0.wireOp",EDGE,"E0")])]}),"instanceName":"15"}),"instanceName":"9"});
            var Q118;
            Q118=makeQuery(id+"F9.opPattern","COPY",BODY,{"derivedFrom":makeQuery(id+"F8.opPattern","COPY",BODY,{"derivedFrom":makeQuery(id+"F4.opExtrude","SWEPT_BODY",BODY,{"disambiguationData":[OSD([sQuery(id+"F0.wireOp",EDGE,"E0")])]}),"instanceName":"1"}),"instanceName":"10"});
            var Q119;
            Q119=makeQuery(id+"F9.opPattern","COPY",BODY,{"derivedFrom":makeQuery(id+"F8.opPattern","COPY",BODY,{"derivedFrom":makeQuery(id+"F4.opExtrude","SWEPT_BODY",BODY,{"disambiguationData":[OSD([sQuery(id+"F0.wireOp",EDGE,"E0")])]}),"instanceName":"2"}),"instanceName":"10"});
            var Q120;
            Q120=makeQuery(id+"F9.opPattern","COPY",BODY,{"derivedFrom":makeQuery(id+"F8.opPattern","COPY",BODY,{"derivedFrom":makeQuery(id+"F4.opExtrude","SWEPT_BODY",BODY,{"disambiguationData":[OSD([sQuery(id+"F0.wireOp",EDGE,"E0")])]}),"instanceName":"3"}),"instanceName":"10"});
            var Q121;
            Q121=makeQuery(id+"F9.opPattern","COPY",BODY,{"derivedFrom":makeQuery(id+"F8.opPattern","COPY",BODY,{"derivedFrom":makeQuery(id+"F4.opExtrude","SWEPT_BODY",BODY,{"disambiguationData":[OSD([sQuery(id+"F0.wireOp",EDGE,"E0")])]}),"instanceName":"9"}),"instanceName":"10"});
            var Q122;
            Q122=makeQuery(id+"F9.opPattern","COPY",BODY,{"derivedFrom":makeQuery(id+"F8.opPattern","COPY",BODY,{"derivedFrom":makeQuery(id+"F4.opExtrude","SWEPT_BODY",BODY,{"disambiguationData":[OSD([sQuery(id+"F0.wireOp",EDGE,"E0")])]}),"instanceName":"11"}),"instanceName":"10"});
            var Q123;
            Q123=makeQuery(id+"F9.opPattern","COPY",BODY,{"derivedFrom":makeQuery(id+"F8.opPattern","COPY",BODY,{"derivedFrom":makeQuery(id+"F4.opExtrude","SWEPT_BODY",BODY,{"disambiguationData":[OSD([sQuery(id+"F0.wireOp",EDGE,"E0")])]}),"instanceName":"13"}),"instanceName":"10"});
            var Q124;
            Q124=makeQuery(id+"F9.opPattern","COPY",BODY,{"derivedFrom":makeQuery(id+"F8.opPattern","COPY",BODY,{"derivedFrom":makeQuery(id+"F4.opExtrude","SWEPT_BODY",BODY,{"disambiguationData":[OSD([sQuery(id+"F0.wireOp",EDGE,"E0")])]}),"instanceName":"1"}),"instanceName":"11"});
            var Q125;
            Q125=makeQuery(id+"F9.opPattern","COPY",BODY,{"derivedFrom":makeQuery(id+"F8.opPattern","COPY",BODY,{"derivedFrom":makeQuery(id+"F4.opExtrude","SWEPT_BODY",BODY,{"disambiguationData":[OSD([sQuery(id+"F0.wireOp",EDGE,"E0")])]}),"instanceName":"7"}),"instanceName":"11"});
            var Q126;
            Q126=makeQuery(id+"F9.opPattern","COPY",BODY,{"derivedFrom":makeQuery(id+"F8.opPattern","COPY",BODY,{"derivedFrom":makeQuery(id+"F4.opExtrude","SWEPT_BODY",BODY,{"disambiguationData":[OSD([sQuery(id+"F0.wireOp",EDGE,"E0")])]}),"instanceName":"10"}),"instanceName":"11"});
            var Q127;
            Q127=makeQuery(id+"F9.opPattern","COPY",BODY,{"derivedFrom":makeQuery(id+"F8.opPattern","COPY",BODY,{"derivedFrom":makeQuery(id+"F4.opExtrude","SWEPT_BODY",BODY,{"disambiguationData":[OSD([sQuery(id+"F0.wireOp",EDGE,"E0")])]}),"instanceName":"13"}),"instanceName":"11"});
            var Q128;
            Q128=makeQuery(id+"F9.opPattern","COPY",BODY,{"derivedFrom":makeQuery(id+"F8.opPattern","COPY",BODY,{"derivedFrom":makeQuery(id+"F4.opExtrude","SWEPT_BODY",BODY,{"disambiguationData":[OSD([sQuery(id+"F0.wireOp",EDGE,"E0")])]}),"instanceName":"7"}),"instanceName":"12"});
            var Q129;
            Q129=makeQuery(id+"F9.opPattern","COPY",BODY,{"derivedFrom":makeQuery(id+"F8.opPattern","COPY",BODY,{"derivedFrom":makeQuery(id+"F4.opExtrude","SWEPT_BODY",BODY,{"disambiguationData":[OSD([sQuery(id+"F0.wireOp",EDGE,"E0")])]}),"instanceName":"9"}),"instanceName":"12"});
            var Q130;
            Q130=makeQuery(id+"F9.opPattern","COPY",BODY,{"derivedFrom":makeQuery(id+"F8.opPattern","COPY",BODY,{"derivedFrom":makeQuery(id+"F4.opExtrude","SWEPT_BODY",BODY,{"disambiguationData":[OSD([sQuery(id+"F0.wireOp",EDGE,"E0")])]}),"instanceName":"1"}),"instanceName":"13"});
            var Q131;
            Q131=makeQuery(id+"F9.opPattern","COPY",BODY,{"derivedFrom":makeQuery(id+"F8.opPattern","COPY",BODY,{"derivedFrom":makeQuery(id+"F4.opExtrude","SWEPT_BODY",BODY,{"disambiguationData":[OSD([sQuery(id+"F0.wireOp",EDGE,"E0")])]}),"instanceName":"3"}),"instanceName":"13"});
            var Q132;
            Q132=makeQuery(id+"F9.opPattern","COPY",BODY,{"derivedFrom":makeQuery(id+"F8.opPattern","COPY",BODY,{"derivedFrom":makeQuery(id+"F4.opExtrude","SWEPT_BODY",BODY,{"disambiguationData":[OSD([sQuery(id+"F0.wireOp",EDGE,"E0")])]}),"instanceName":"5"}),"instanceName":"13"});
            var Q133;
            Q133=makeQuery(id+"F9.opPattern","COPY",BODY,{"derivedFrom":makeQuery(id+"F8.opPattern","COPY",BODY,{"derivedFrom":makeQuery(id+"F4.opExtrude","SWEPT_BODY",BODY,{"disambiguationData":[OSD([sQuery(id+"F0.wireOp",EDGE,"E0")])]}),"instanceName":"10"}),"instanceName":"13"});
            var Q134;
            Q134=makeQuery(id+"F9.opPattern","COPY",BODY,{"derivedFrom":makeQuery(id+"F8.opPattern","COPY",BODY,{"derivedFrom":makeQuery(id+"F4.opExtrude","SWEPT_BODY",BODY,{"disambiguationData":[OSD([sQuery(id+"F0.wireOp",EDGE,"E0")])]}),"instanceName":"1"}),"instanceName":"14"});
            var Q135;
            Q135=makeQuery(id+"F9.opPattern","COPY",BODY,{"derivedFrom":makeQuery(id+"F8.opPattern","COPY",BODY,{"derivedFrom":makeQuery(id+"F4.opExtrude","SWEPT_BODY",BODY,{"disambiguationData":[OSD([sQuery(id+"F0.wireOp",EDGE,"E0")])]}),"instanceName":"2"}),"instanceName":"14"});
            var Q136;
            Q136=makeQuery(id+"F9.opPattern","COPY",BODY,{"derivedFrom":makeQuery(id+"F8.opPattern","COPY",BODY,{"derivedFrom":makeQuery(id+"F4.opExtrude","SWEPT_BODY",BODY,{"disambiguationData":[OSD([sQuery(id+"F0.wireOp",EDGE,"E0")])]}),"instanceName":"3"}),"instanceName":"14"});
            var Q137;
            Q137=makeQuery(id+"F9.opPattern","COPY",BODY,{"derivedFrom":makeQuery(id+"F8.opPattern","COPY",BODY,{"derivedFrom":makeQuery(id+"F4.opExtrude","SWEPT_BODY",BODY,{"disambiguationData":[OSD([sQuery(id+"F0.wireOp",EDGE,"E0")])]}),"instanceName":"5"}),"instanceName":"14"});
            var Q138;
            Q138=makeQuery(id+"F9.opPattern","COPY",BODY,{"derivedFrom":makeQuery(id+"F8.opPattern","COPY",BODY,{"derivedFrom":makeQuery(id+"F4.opExtrude","SWEPT_BODY",BODY,{"disambiguationData":[OSD([sQuery(id+"F0.wireOp",EDGE,"E0")])]}),"instanceName":"6"}),"instanceName":"14"});
            var Q139;
            Q139=makeQuery(id+"F9.opPattern","COPY",BODY,{"derivedFrom":makeQuery(id+"F8.opPattern","COPY",BODY,{"derivedFrom":makeQuery(id+"F4.opExtrude","SWEPT_BODY",BODY,{"disambiguationData":[OSD([sQuery(id+"F0.wireOp",EDGE,"E0")])]}),"instanceName":"9"}),"instanceName":"14"});
            var Q140;
            Q140=makeQuery(id+"F9.opPattern","COPY",BODY,{"derivedFrom":makeQuery(id+"F8.opPattern","COPY",BODY,{"derivedFrom":makeQuery(id+"F4.opExtrude","SWEPT_BODY",BODY,{"disambiguationData":[OSD([sQuery(id+"F0.wireOp",EDGE,"E0")])]}),"instanceName":"10"}),"instanceName":"14"});
            var Q141;
            Q141=makeQuery(id+"F9.opPattern","COPY",BODY,{"derivedFrom":makeQuery(id+"F8.opPattern","COPY",BODY,{"derivedFrom":makeQuery(id+"F4.opExtrude","SWEPT_BODY",BODY,{"disambiguationData":[OSD([sQuery(id+"F0.wireOp",EDGE,"E0")])]}),"instanceName":"1"}),"instanceName":"15"});
            var Q142;
            Q142=makeQuery(id+"F9.opPattern","COPY",BODY,{"derivedFrom":makeQuery(id+"F8.opPattern","COPY",BODY,{"derivedFrom":makeQuery(id+"F4.opExtrude","SWEPT_BODY",BODY,{"disambiguationData":[OSD([sQuery(id+"F0.wireOp",EDGE,"E0")])]}),"instanceName":"2"}),"instanceName":"15"});
            var Q143;
            Q143=makeQuery(id+"F9.opPattern","COPY",BODY,{"derivedFrom":makeQuery(id+"F8.opPattern","COPY",BODY,{"derivedFrom":makeQuery(id+"F4.opExtrude","SWEPT_BODY",BODY,{"disambiguationData":[OSD([sQuery(id+"F0.wireOp",EDGE,"E0")])]}),"instanceName":"3"}),"instanceName":"15"});
            var Q144;
            Q144=makeQuery(id+"F9.opPattern","COPY",BODY,{"derivedFrom":makeQuery(id+"F8.opPattern","COPY",BODY,{"derivedFrom":makeQuery(id+"F4.opExtrude","SWEPT_BODY",BODY,{"disambiguationData":[OSD([sQuery(id+"F0.wireOp",EDGE,"E0")])]}),"instanceName":"5"}),"instanceName":"15"});
            var Q145;
            Q145=makeQuery(id+"F9.opPattern","COPY",BODY,{"derivedFrom":makeQuery(id+"F8.opPattern","COPY",BODY,{"derivedFrom":makeQuery(id+"F4.opExtrude","SWEPT_BODY",BODY,{"disambiguationData":[OSD([sQuery(id+"F0.wireOp",EDGE,"E0")])]}),"instanceName":"9"}),"instanceName":"15"});
            var Q146;
            Q146=makeQuery(id+"F9.opPattern","COPY",BODY,{"derivedFrom":makeQuery(id+"F8.opPattern","COPY",BODY,{"derivedFrom":makeQuery(id+"F4.opExtrude","SWEPT_BODY",BODY,{"disambiguationData":[OSD([sQuery(id+"F0.wireOp",EDGE,"E0")])]}),"instanceName":"10"}),"instanceName":"15"});
            var Q147;
            Q147=makeQuery(id+"F9.opPattern","COPY",BODY,{"derivedFrom":makeQuery(id+"F8.opPattern","COPY",BODY,{"derivedFrom":makeQuery(id+"F4.opExtrude","SWEPT_BODY",BODY,{"disambiguationData":[OSD([sQuery(id+"F0.wireOp",EDGE,"E0")])]}),"instanceName":"11"}),"instanceName":"15"});
            var Q148;
            Q148=makeQuery(id+"F8.opPattern","COPY",BODY,{"derivedFrom":makeQuery(id+"F4.opExtrude","SWEPT_BODY",BODY,{"disambiguationData":[OSD([sQuery(id+"F0.wireOp",EDGE,"E0")])]}),"instanceName":"4"});
            var Q149;
            Q149=makeQuery(id+"F9.opPattern","COPY",BODY,{"derivedFrom":makeQuery(id+"F8.opPattern","COPY",BODY,{"derivedFrom":makeQuery(id+"F4.opExtrude","SWEPT_BODY",BODY,{"disambiguationData":[OSD([sQuery(id+"F0.wireOp",EDGE,"E0")])]}),"instanceName":"12"}),"instanceName":"7"});
            var Q150;
            Q150=makeQuery(id+"F9.opPattern","COPY",BODY,{"derivedFrom":makeQuery(id+"F8.opPattern","COPY",BODY,{"derivedFrom":makeQuery(id+"F4.opExtrude","SWEPT_BODY",BODY,{"disambiguationData":[OSD([sQuery(id+"F0.wireOp",EDGE,"E0")])]}),"instanceName":"8"}),"instanceName":"7"});
            var Q151;
            Q151=makeQuery(id+"F9.opPattern","COPY",BODY,{"derivedFrom":makeQuery(id+"F4.opExtrude","SWEPT_BODY",BODY,{"disambiguationData":[OSD([sQuery(id+"F0.wireOp",EDGE,"E0")])]}),"instanceName":"7"});
            var Q152;
            Q152=makeQuery(id+"F9.opPattern","COPY",BODY,{"derivedFrom":makeQuery(id+"F8.opPattern","COPY",BODY,{"derivedFrom":makeQuery(id+"F4.opExtrude","SWEPT_BODY",BODY,{"disambiguationData":[OSD([sQuery(id+"F0.wireOp",EDGE,"E0")])]}),"instanceName":"14"}),"instanceName":"6"});
            var Q153;
            Q153=makeQuery(id+"F9.opPattern","COPY",BODY,{"derivedFrom":makeQuery(id+"F8.opPattern","COPY",BODY,{"derivedFrom":makeQuery(id+"F4.opExtrude","SWEPT_BODY",BODY,{"disambiguationData":[OSD([sQuery(id+"F0.wireOp",EDGE,"E0")])]}),"instanceName":"12"}),"instanceName":"6"});
            var Q154;
            Q154=makeQuery(id+"F9.opPattern","COPY",BODY,{"derivedFrom":makeQuery(id+"F8.opPattern","COPY",BODY,{"derivedFrom":makeQuery(id+"F4.opExtrude","SWEPT_BODY",BODY,{"disambiguationData":[OSD([sQuery(id+"F0.wireOp",EDGE,"E0")])]}),"instanceName":"8"}),"instanceName":"6"});
            var Q155;
            Q155=makeQuery(id+"F9.opPattern","COPY",BODY,{"derivedFrom":makeQuery(id+"F8.opPattern","COPY",BODY,{"derivedFrom":makeQuery(id+"F4.opExtrude","SWEPT_BODY",BODY,{"disambiguationData":[OSD([sQuery(id+"F0.wireOp",EDGE,"E0")])]}),"instanceName":"4"}),"instanceName":"6"});
            var Q156;
            Q156=makeQuery(id+"F9.opPattern","COPY",BODY,{"derivedFrom":makeQuery(id+"F8.opPattern","COPY",BODY,{"derivedFrom":makeQuery(id+"F4.opExtrude","SWEPT_BODY",BODY,{"disambiguationData":[OSD([sQuery(id+"F0.wireOp",EDGE,"E0")])]}),"instanceName":"15"}),"instanceName":"5"});
            var Q157;
            Q157=makeQuery(id+"F9.opPattern","COPY",BODY,{"derivedFrom":makeQuery(id+"F8.opPattern","COPY",BODY,{"derivedFrom":makeQuery(id+"F4.opExtrude","SWEPT_BODY",BODY,{"disambiguationData":[OSD([sQuery(id+"F0.wireOp",EDGE,"E0")])]}),"instanceName":"12"}),"instanceName":"5"});
            var Q158;
            Q158=makeQuery(id+"F9.opPattern","COPY",BODY,{"derivedFrom":makeQuery(id+"F8.opPattern","COPY",BODY,{"derivedFrom":makeQuery(id+"F4.opExtrude","SWEPT_BODY",BODY,{"disambiguationData":[OSD([sQuery(id+"F0.wireOp",EDGE,"E0")])]}),"instanceName":"4"}),"instanceName":"5"});
            var Q159;
            Q159=makeQuery(id+"F9.opPattern","COPY",BODY,{"derivedFrom":makeQuery(id+"F8.opPattern","COPY",BODY,{"derivedFrom":makeQuery(id+"F4.opExtrude","SWEPT_BODY",BODY,{"disambiguationData":[OSD([sQuery(id+"F0.wireOp",EDGE,"E0")])]}),"instanceName":"15"}),"instanceName":"4"});
            var Q160;
            Q160=makeQuery(id+"F9.opPattern","COPY",BODY,{"derivedFrom":makeQuery(id+"F8.opPattern","COPY",BODY,{"derivedFrom":makeQuery(id+"F4.opExtrude","SWEPT_BODY",BODY,{"disambiguationData":[OSD([sQuery(id+"F0.wireOp",EDGE,"E0")])]}),"instanceName":"14"}),"instanceName":"4"});
            var Q161;
            Q161=makeQuery(id+"F9.opPattern","COPY",BODY,{"derivedFrom":makeQuery(id+"F8.opPattern","COPY",BODY,{"derivedFrom":makeQuery(id+"F4.opExtrude","SWEPT_BODY",BODY,{"disambiguationData":[OSD([sQuery(id+"F0.wireOp",EDGE,"E0")])]}),"instanceName":"4"}),"instanceName":"4"});
            var Q162;
            Q162=makeQuery(id+"F9.opPattern","COPY",BODY,{"derivedFrom":makeQuery(id+"F4.opExtrude","SWEPT_BODY",BODY,{"disambiguationData":[OSD([sQuery(id+"F0.wireOp",EDGE,"E0")])]}),"instanceName":"4"});
            var Q163;
            Q163=makeQuery(id+"F9.opPattern","COPY",BODY,{"derivedFrom":makeQuery(id+"F8.opPattern","COPY",BODY,{"derivedFrom":makeQuery(id+"F4.opExtrude","SWEPT_BODY",BODY,{"disambiguationData":[OSD([sQuery(id+"F0.wireOp",EDGE,"E0")])]}),"instanceName":"12"}),"instanceName":"3"});
            var Q164;
            Q164=makeQuery(id+"F9.opPattern","COPY",BODY,{"derivedFrom":makeQuery(id+"F8.opPattern","COPY",BODY,{"derivedFrom":makeQuery(id+"F4.opExtrude","SWEPT_BODY",BODY,{"disambiguationData":[OSD([sQuery(id+"F0.wireOp",EDGE,"E0")])]}),"instanceName":"15"}),"instanceName":"2"});
            var Q165;
            Q165=makeQuery(id+"F9.opPattern","COPY",BODY,{"derivedFrom":makeQuery(id+"F8.opPattern","COPY",BODY,{"derivedFrom":makeQuery(id+"F4.opExtrude","SWEPT_BODY",BODY,{"disambiguationData":[OSD([sQuery(id+"F0.wireOp",EDGE,"E0")])]}),"instanceName":"13"}),"instanceName":"1"});
            var Q166;
            Q166=makeQuery(id+"F8.opPattern","COPY",BODY,{"derivedFrom":makeQuery(id+"F4.opExtrude","SWEPT_BODY",BODY,{"disambiguationData":[OSD([sQuery(id+"F0.wireOp",EDGE,"E0")])]}),"instanceName":"14"});
            var Q167;
            Q167=makeQuery(id+"F8.opPattern","COPY",BODY,{"derivedFrom":makeQuery(id+"F4.opExtrude","SWEPT_BODY",BODY,{"disambiguationData":[OSD([sQuery(id+"F0.wireOp",EDGE,"E0")])]}),"instanceName":"12"});
            var Q168;
            Q168=makeQuery(id+"F8.opPattern","COPY",BODY,{"derivedFrom":makeQuery(id+"F4.opExtrude","SWEPT_BODY",BODY,{"disambiguationData":[OSD([sQuery(id+"F0.wireOp",EDGE,"E0")])]}),"instanceName":"8"});
            var Q169;
            Q169=makeQuery(id+"F9.opPattern","COPY",BODY,{"derivedFrom":makeQuery(id+"F8.opPattern","COPY",BODY,{"derivedFrom":makeQuery(id+"F4.opExtrude","SWEPT_BODY",BODY,{"disambiguationData":[OSD([sQuery(id+"F0.wireOp",EDGE,"E0")])]}),"instanceName":"5"}),"instanceName":"8"});
            var Q170;
            Q170=makeQuery(id+"F9.opPattern","COPY",BODY,{"derivedFrom":makeQuery(id+"F8.opPattern","COPY",BODY,{"derivedFrom":makeQuery(id+"F4.opExtrude","SWEPT_BODY",BODY,{"disambiguationData":[OSD([sQuery(id+"F0.wireOp",EDGE,"E0")])]}),"instanceName":"7"}),"instanceName":"8"});
            var Q171;
            Q171=makeQuery(id+"F9.opPattern","COPY",BODY,{"derivedFrom":makeQuery(id+"F8.opPattern","COPY",BODY,{"derivedFrom":makeQuery(id+"F4.opExtrude","SWEPT_BODY",BODY,{"disambiguationData":[OSD([sQuery(id+"F0.wireOp",EDGE,"E0")])]}),"instanceName":"9"}),"instanceName":"8"});
            var Q172;
            Q172=makeQuery(id+"F9.opPattern","COPY",BODY,{"derivedFrom":makeQuery(id+"F8.opPattern","COPY",BODY,{"derivedFrom":makeQuery(id+"F4.opExtrude","SWEPT_BODY",BODY,{"disambiguationData":[OSD([sQuery(id+"F0.wireOp",EDGE,"E0")])]}),"instanceName":"11"}),"instanceName":"8"});
            var Q173;
            Q173=makeQuery(id+"F9.opPattern","COPY",BODY,{"derivedFrom":makeQuery(id+"F8.opPattern","COPY",BODY,{"derivedFrom":makeQuery(id+"F4.opExtrude","SWEPT_BODY",BODY,{"disambiguationData":[OSD([sQuery(id+"F0.wireOp",EDGE,"E0")])]}),"instanceName":"13"}),"instanceName":"8"});
            var Q174;
            Q174=makeQuery(id+"F9.opPattern","COPY",BODY,{"derivedFrom":makeQuery(id+"F8.opPattern","COPY",BODY,{"derivedFrom":makeQuery(id+"F4.opExtrude","SWEPT_BODY",BODY,{"disambiguationData":[OSD([sQuery(id+"F0.wireOp",EDGE,"E0")])]}),"instanceName":"14"}),"instanceName":"8"});
            var Q175;
            Q175=makeQuery(id+"F9.opPattern","COPY",BODY,{"derivedFrom":makeQuery(id+"F8.opPattern","COPY",BODY,{"derivedFrom":makeQuery(id+"F4.opExtrude","SWEPT_BODY",BODY,{"disambiguationData":[OSD([sQuery(id+"F0.wireOp",EDGE,"E0")])]}),"instanceName":"15"}),"instanceName":"8"});
            var Q176;
            Q176=makeQuery(id+"F9.opPattern","COPY",BODY,{"derivedFrom":makeQuery(id+"F4.opExtrude","SWEPT_BODY",BODY,{"disambiguationData":[OSD([sQuery(id+"F0.wireOp",EDGE,"E0")])]}),"instanceName":"9"});
            var Q177;
            Q177=makeQuery(id+"F9.opPattern","COPY",BODY,{"derivedFrom":makeQuery(id+"F8.opPattern","COPY",BODY,{"derivedFrom":makeQuery(id+"F4.opExtrude","SWEPT_BODY",BODY,{"disambiguationData":[OSD([sQuery(id+"F0.wireOp",EDGE,"E0")])]}),"instanceName":"5"}),"instanceName":"9"});
            var Q178;
            Q178=makeQuery(id+"F9.opPattern","COPY",BODY,{"derivedFrom":makeQuery(id+"F8.opPattern","COPY",BODY,{"derivedFrom":makeQuery(id+"F4.opExtrude","SWEPT_BODY",BODY,{"disambiguationData":[OSD([sQuery(id+"F0.wireOp",EDGE,"E0")])]}),"instanceName":"8"}),"instanceName":"9"});
            var Q179;
            Q179=makeQuery(id+"F9.opPattern","COPY",BODY,{"derivedFrom":makeQuery(id+"F8.opPattern","COPY",BODY,{"derivedFrom":makeQuery(id+"F4.opExtrude","SWEPT_BODY",BODY,{"disambiguationData":[OSD([sQuery(id+"F0.wireOp",EDGE,"E0")])]}),"instanceName":"9"}),"instanceName":"9"});
            var Q180;
            Q180=makeQuery(id+"F9.opPattern","COPY",BODY,{"derivedFrom":makeQuery(id+"F8.opPattern","COPY",BODY,{"derivedFrom":makeQuery(id+"F4.opExtrude","SWEPT_BODY",BODY,{"disambiguationData":[OSD([sQuery(id+"F0.wireOp",EDGE,"E0")])]}),"instanceName":"10"}),"instanceName":"9"});
            var Q181;
            Q181=makeQuery(id+"F9.opPattern","COPY",BODY,{"derivedFrom":makeQuery(id+"F8.opPattern","COPY",BODY,{"derivedFrom":makeQuery(id+"F4.opExtrude","SWEPT_BODY",BODY,{"disambiguationData":[OSD([sQuery(id+"F0.wireOp",EDGE,"E0")])]}),"instanceName":"11"}),"instanceName":"9"});
            var Q182;
            Q182=makeQuery(id+"F9.opPattern","COPY",BODY,{"derivedFrom":makeQuery(id+"F8.opPattern","COPY",BODY,{"derivedFrom":makeQuery(id+"F4.opExtrude","SWEPT_BODY",BODY,{"disambiguationData":[OSD([sQuery(id+"F0.wireOp",EDGE,"E0")])]}),"instanceName":"12"}),"instanceName":"9"});
            var Q183;
            Q183=makeQuery(id+"F9.opPattern","COPY",BODY,{"derivedFrom":makeQuery(id+"F8.opPattern","COPY",BODY,{"derivedFrom":makeQuery(id+"F4.opExtrude","SWEPT_BODY",BODY,{"disambiguationData":[OSD([sQuery(id+"F0.wireOp",EDGE,"E0")])]}),"instanceName":"13"}),"instanceName":"9"});
            var Q184;
            Q184=makeQuery(id+"F9.opPattern","COPY",BODY,{"derivedFrom":makeQuery(id+"F4.opExtrude","SWEPT_BODY",BODY,{"disambiguationData":[OSD([sQuery(id+"F0.wireOp",EDGE,"E0")])]}),"instanceName":"10"});
            var Q185;
            Q185=makeQuery(id+"F9.opPattern","COPY",BODY,{"derivedFrom":makeQuery(id+"F8.opPattern","COPY",BODY,{"derivedFrom":makeQuery(id+"F4.opExtrude","SWEPT_BODY",BODY,{"disambiguationData":[OSD([sQuery(id+"F0.wireOp",EDGE,"E0")])]}),"instanceName":"5"}),"instanceName":"10"});
            var Q186;
            Q186=makeQuery(id+"F9.opPattern","COPY",BODY,{"derivedFrom":makeQuery(id+"F8.opPattern","COPY",BODY,{"derivedFrom":makeQuery(id+"F4.opExtrude","SWEPT_BODY",BODY,{"disambiguationData":[OSD([sQuery(id+"F0.wireOp",EDGE,"E0")])]}),"instanceName":"6"}),"instanceName":"10"});
            var Q187;
            Q187=makeQuery(id+"F9.opPattern","COPY",BODY,{"derivedFrom":makeQuery(id+"F8.opPattern","COPY",BODY,{"derivedFrom":makeQuery(id+"F4.opExtrude","SWEPT_BODY",BODY,{"disambiguationData":[OSD([sQuery(id+"F0.wireOp",EDGE,"E0")])]}),"instanceName":"7"}),"instanceName":"10"});
            var Q188;
            Q188=makeQuery(id+"F9.opPattern","COPY",BODY,{"derivedFrom":makeQuery(id+"F8.opPattern","COPY",BODY,{"derivedFrom":makeQuery(id+"F4.opExtrude","SWEPT_BODY",BODY,{"disambiguationData":[OSD([sQuery(id+"F0.wireOp",EDGE,"E0")])]}),"instanceName":"10"}),"instanceName":"10"});
            var Q189;
            Q189=makeQuery(id+"F9.opPattern","COPY",BODY,{"derivedFrom":makeQuery(id+"F8.opPattern","COPY",BODY,{"derivedFrom":makeQuery(id+"F4.opExtrude","SWEPT_BODY",BODY,{"disambiguationData":[OSD([sQuery(id+"F0.wireOp",EDGE,"E0")])]}),"instanceName":"12"}),"instanceName":"10"});
            var Q190;
            Q190=makeQuery(id+"F9.opPattern","COPY",BODY,{"derivedFrom":makeQuery(id+"F8.opPattern","COPY",BODY,{"derivedFrom":makeQuery(id+"F4.opExtrude","SWEPT_BODY",BODY,{"disambiguationData":[OSD([sQuery(id+"F0.wireOp",EDGE,"E0")])]}),"instanceName":"14"}),"instanceName":"10"});
            var Q191;
            Q191=makeQuery(id+"F9.opPattern","COPY",BODY,{"derivedFrom":makeQuery(id+"F8.opPattern","COPY",BODY,{"derivedFrom":makeQuery(id+"F4.opExtrude","SWEPT_BODY",BODY,{"disambiguationData":[OSD([sQuery(id+"F0.wireOp",EDGE,"E0")])]}),"instanceName":"15"}),"instanceName":"10"});
            var Q192;
            Q192=makeQuery(id+"F9.opPattern","COPY",BODY,{"derivedFrom":makeQuery(id+"F4.opExtrude","SWEPT_BODY",BODY,{"disambiguationData":[OSD([sQuery(id+"F0.wireOp",EDGE,"E0")])]}),"instanceName":"11"});
            var Q193;
            Q193=makeQuery(id+"F9.opPattern","COPY",BODY,{"derivedFrom":makeQuery(id+"F8.opPattern","COPY",BODY,{"derivedFrom":makeQuery(id+"F4.opExtrude","SWEPT_BODY",BODY,{"disambiguationData":[OSD([sQuery(id+"F0.wireOp",EDGE,"E0")])]}),"instanceName":"2"}),"instanceName":"11"});
            var Q194;
            Q194=makeQuery(id+"F9.opPattern","COPY",BODY,{"derivedFrom":makeQuery(id+"F8.opPattern","COPY",BODY,{"derivedFrom":makeQuery(id+"F4.opExtrude","SWEPT_BODY",BODY,{"disambiguationData":[OSD([sQuery(id+"F0.wireOp",EDGE,"E0")])]}),"instanceName":"3"}),"instanceName":"11"});
            var Q195;
            Q195=makeQuery(id+"F9.opPattern","COPY",BODY,{"derivedFrom":makeQuery(id+"F8.opPattern","COPY",BODY,{"derivedFrom":makeQuery(id+"F4.opExtrude","SWEPT_BODY",BODY,{"disambiguationData":[OSD([sQuery(id+"F0.wireOp",EDGE,"E0")])]}),"instanceName":"4"}),"instanceName":"11"});
            var Q196;
            Q196=makeQuery(id+"F9.opPattern","COPY",BODY,{"derivedFrom":makeQuery(id+"F8.opPattern","COPY",BODY,{"derivedFrom":makeQuery(id+"F4.opExtrude","SWEPT_BODY",BODY,{"disambiguationData":[OSD([sQuery(id+"F0.wireOp",EDGE,"E0")])]}),"instanceName":"5"}),"instanceName":"11"});
            var Q197;
            Q197=makeQuery(id+"F9.opPattern","COPY",BODY,{"derivedFrom":makeQuery(id+"F8.opPattern","COPY",BODY,{"derivedFrom":makeQuery(id+"F4.opExtrude","SWEPT_BODY",BODY,{"disambiguationData":[OSD([sQuery(id+"F0.wireOp",EDGE,"E0")])]}),"instanceName":"6"}),"instanceName":"11"});
            var Q198;
            Q198=makeQuery(id+"F9.opPattern","COPY",BODY,{"derivedFrom":makeQuery(id+"F8.opPattern","COPY",BODY,{"derivedFrom":makeQuery(id+"F4.opExtrude","SWEPT_BODY",BODY,{"disambiguationData":[OSD([sQuery(id+"F0.wireOp",EDGE,"E0")])]}),"instanceName":"8"}),"instanceName":"11"});
            var Q199;
            Q199=makeQuery(id+"F9.opPattern","COPY",BODY,{"derivedFrom":makeQuery(id+"F8.opPattern","COPY",BODY,{"derivedFrom":makeQuery(id+"F4.opExtrude","SWEPT_BODY",BODY,{"disambiguationData":[OSD([sQuery(id+"F0.wireOp",EDGE,"E0")])]}),"instanceName":"9"}),"instanceName":"11"});
            var Q200;
            Q200=makeQuery(id+"F9.opPattern","COPY",BODY,{"derivedFrom":makeQuery(id+"F8.opPattern","COPY",BODY,{"derivedFrom":makeQuery(id+"F4.opExtrude","SWEPT_BODY",BODY,{"disambiguationData":[OSD([sQuery(id+"F0.wireOp",EDGE,"E0")])]}),"instanceName":"11"}),"instanceName":"11"});
            var Q201;
            Q201=makeQuery(id+"F9.opPattern","COPY",BODY,{"derivedFrom":makeQuery(id+"F8.opPattern","COPY",BODY,{"derivedFrom":makeQuery(id+"F4.opExtrude","SWEPT_BODY",BODY,{"disambiguationData":[OSD([sQuery(id+"F0.wireOp",EDGE,"E0")])]}),"instanceName":"14"}),"instanceName":"11"});
            var Q202;
            Q202=makeQuery(id+"F9.opPattern","COPY",BODY,{"derivedFrom":makeQuery(id+"F8.opPattern","COPY",BODY,{"derivedFrom":makeQuery(id+"F4.opExtrude","SWEPT_BODY",BODY,{"disambiguationData":[OSD([sQuery(id+"F0.wireOp",EDGE,"E0")])]}),"instanceName":"15"}),"instanceName":"11"});
            var Q203;
            Q203=makeQuery(id+"F9.opPattern","COPY",BODY,{"derivedFrom":makeQuery(id+"F8.opPattern","COPY",BODY,{"derivedFrom":makeQuery(id+"F4.opExtrude","SWEPT_BODY",BODY,{"disambiguationData":[OSD([sQuery(id+"F0.wireOp",EDGE,"E0")])]}),"instanceName":"1"}),"instanceName":"12"});
            var Q204;
            Q204=makeQuery(id+"F9.opPattern","COPY",BODY,{"derivedFrom":makeQuery(id+"F8.opPattern","COPY",BODY,{"derivedFrom":makeQuery(id+"F4.opExtrude","SWEPT_BODY",BODY,{"disambiguationData":[OSD([sQuery(id+"F0.wireOp",EDGE,"E0")])]}),"instanceName":"2"}),"instanceName":"12"});
            var Q205;
            Q205=makeQuery(id+"F9.opPattern","COPY",BODY,{"derivedFrom":makeQuery(id+"F8.opPattern","COPY",BODY,{"derivedFrom":makeQuery(id+"F4.opExtrude","SWEPT_BODY",BODY,{"disambiguationData":[OSD([sQuery(id+"F0.wireOp",EDGE,"E0")])]}),"instanceName":"3"}),"instanceName":"12"});
            var Q206;
            Q206=makeQuery(id+"F9.opPattern","COPY",BODY,{"derivedFrom":makeQuery(id+"F8.opPattern","COPY",BODY,{"derivedFrom":makeQuery(id+"F4.opExtrude","SWEPT_BODY",BODY,{"disambiguationData":[OSD([sQuery(id+"F0.wireOp",EDGE,"E0")])]}),"instanceName":"5"}),"instanceName":"12"});
            var Q207;
            Q207=makeQuery(id+"F9.opPattern","COPY",BODY,{"derivedFrom":makeQuery(id+"F8.opPattern","COPY",BODY,{"derivedFrom":makeQuery(id+"F4.opExtrude","SWEPT_BODY",BODY,{"disambiguationData":[OSD([sQuery(id+"F0.wireOp",EDGE,"E0")])]}),"instanceName":"6"}),"instanceName":"12"});
            var Q208;
            Q208=makeQuery(id+"F9.opPattern","COPY",BODY,{"derivedFrom":makeQuery(id+"F8.opPattern","COPY",BODY,{"derivedFrom":makeQuery(id+"F4.opExtrude","SWEPT_BODY",BODY,{"disambiguationData":[OSD([sQuery(id+"F0.wireOp",EDGE,"E0")])]}),"instanceName":"10"}),"instanceName":"12"});
            var Q209;
            Q209=makeQuery(id+"F9.opPattern","COPY",BODY,{"derivedFrom":makeQuery(id+"F8.opPattern","COPY",BODY,{"derivedFrom":makeQuery(id+"F4.opExtrude","SWEPT_BODY",BODY,{"disambiguationData":[OSD([sQuery(id+"F0.wireOp",EDGE,"E0")])]}),"instanceName":"11"}),"instanceName":"12"});
            var Q210;
            Q210=makeQuery(id+"F9.opPattern","COPY",BODY,{"derivedFrom":makeQuery(id+"F8.opPattern","COPY",BODY,{"derivedFrom":makeQuery(id+"F4.opExtrude","SWEPT_BODY",BODY,{"disambiguationData":[OSD([sQuery(id+"F0.wireOp",EDGE,"E0")])]}),"instanceName":"13"}),"instanceName":"12"});
            var Q211;
            Q211=makeQuery(id+"F9.opPattern","COPY",BODY,{"derivedFrom":makeQuery(id+"F8.opPattern","COPY",BODY,{"derivedFrom":makeQuery(id+"F4.opExtrude","SWEPT_BODY",BODY,{"disambiguationData":[OSD([sQuery(id+"F0.wireOp",EDGE,"E0")])]}),"instanceName":"15"}),"instanceName":"12"});
            var Q212;
            Q212=makeQuery(id+"F9.opPattern","COPY",BODY,{"derivedFrom":makeQuery(id+"F4.opExtrude","SWEPT_BODY",BODY,{"disambiguationData":[OSD([sQuery(id+"F0.wireOp",EDGE,"E0")])]}),"instanceName":"13"});
            var Q213;
            Q213=makeQuery(id+"F9.opPattern","COPY",BODY,{"derivedFrom":makeQuery(id+"F8.opPattern","COPY",BODY,{"derivedFrom":makeQuery(id+"F4.opExtrude","SWEPT_BODY",BODY,{"disambiguationData":[OSD([sQuery(id+"F0.wireOp",EDGE,"E0")])]}),"instanceName":"2"}),"instanceName":"13"});
            var Q214;
            Q214=makeQuery(id+"F9.opPattern","COPY",BODY,{"derivedFrom":makeQuery(id+"F8.opPattern","COPY",BODY,{"derivedFrom":makeQuery(id+"F4.opExtrude","SWEPT_BODY",BODY,{"disambiguationData":[OSD([sQuery(id+"F0.wireOp",EDGE,"E0")])]}),"instanceName":"4"}),"instanceName":"13"});
            var Q215;
            Q215=makeQuery(id+"F9.opPattern","COPY",BODY,{"derivedFrom":makeQuery(id+"F8.opPattern","COPY",BODY,{"derivedFrom":makeQuery(id+"F4.opExtrude","SWEPT_BODY",BODY,{"disambiguationData":[OSD([sQuery(id+"F0.wireOp",EDGE,"E0")])]}),"instanceName":"6"}),"instanceName":"13"});
            var Q216;
            Q216=makeQuery(id+"F9.opPattern","COPY",BODY,{"derivedFrom":makeQuery(id+"F8.opPattern","COPY",BODY,{"derivedFrom":makeQuery(id+"F4.opExtrude","SWEPT_BODY",BODY,{"disambiguationData":[OSD([sQuery(id+"F0.wireOp",EDGE,"E0")])]}),"instanceName":"7"}),"instanceName":"13"});
            var Q217;
            Q217=makeQuery(id+"F9.opPattern","COPY",BODY,{"derivedFrom":makeQuery(id+"F8.opPattern","COPY",BODY,{"derivedFrom":makeQuery(id+"F4.opExtrude","SWEPT_BODY",BODY,{"disambiguationData":[OSD([sQuery(id+"F0.wireOp",EDGE,"E0")])]}),"instanceName":"9"}),"instanceName":"13"});
            var Q218;
            Q218=makeQuery(id+"F9.opPattern","COPY",BODY,{"derivedFrom":makeQuery(id+"F8.opPattern","COPY",BODY,{"derivedFrom":makeQuery(id+"F4.opExtrude","SWEPT_BODY",BODY,{"disambiguationData":[OSD([sQuery(id+"F0.wireOp",EDGE,"E0")])]}),"instanceName":"11"}),"instanceName":"13"});
            var Q219;
            Q219=makeQuery(id+"F9.opPattern","COPY",BODY,{"derivedFrom":makeQuery(id+"F8.opPattern","COPY",BODY,{"derivedFrom":makeQuery(id+"F4.opExtrude","SWEPT_BODY",BODY,{"disambiguationData":[OSD([sQuery(id+"F0.wireOp",EDGE,"E0")])]}),"instanceName":"13"}),"instanceName":"13"});
            var Q220;
            Q220=makeQuery(id+"F9.opPattern","COPY",BODY,{"derivedFrom":makeQuery(id+"F8.opPattern","COPY",BODY,{"derivedFrom":makeQuery(id+"F4.opExtrude","SWEPT_BODY",BODY,{"disambiguationData":[OSD([sQuery(id+"F0.wireOp",EDGE,"E0")])]}),"instanceName":"14"}),"instanceName":"13"});
            var Q221;
            Q221=makeQuery(id+"F9.opPattern","COPY",BODY,{"derivedFrom":makeQuery(id+"F8.opPattern","COPY",BODY,{"derivedFrom":makeQuery(id+"F4.opExtrude","SWEPT_BODY",BODY,{"disambiguationData":[OSD([sQuery(id+"F0.wireOp",EDGE,"E0")])]}),"instanceName":"15"}),"instanceName":"13"});
            var Q222;
            Q222=makeQuery(id+"F9.opPattern","COPY",BODY,{"derivedFrom":makeQuery(id+"F8.opPattern","COPY",BODY,{"derivedFrom":makeQuery(id+"F4.opExtrude","SWEPT_BODY",BODY,{"disambiguationData":[OSD([sQuery(id+"F0.wireOp",EDGE,"E0")])]}),"instanceName":"7"}),"instanceName":"14"});
            var Q223;
            Q223=makeQuery(id+"F9.opPattern","COPY",BODY,{"derivedFrom":makeQuery(id+"F8.opPattern","COPY",BODY,{"derivedFrom":makeQuery(id+"F4.opExtrude","SWEPT_BODY",BODY,{"disambiguationData":[OSD([sQuery(id+"F0.wireOp",EDGE,"E0")])]}),"instanceName":"11"}),"instanceName":"14"});
            var Q224;
            Q224=makeQuery(id+"F9.opPattern","COPY",BODY,{"derivedFrom":makeQuery(id+"F8.opPattern","COPY",BODY,{"derivedFrom":makeQuery(id+"F4.opExtrude","SWEPT_BODY",BODY,{"disambiguationData":[OSD([sQuery(id+"F0.wireOp",EDGE,"E0")])]}),"instanceName":"13"}),"instanceName":"14"});
            var Q225;
            Q225=makeQuery(id+"F9.opPattern","COPY",BODY,{"derivedFrom":makeQuery(id+"F8.opPattern","COPY",BODY,{"derivedFrom":makeQuery(id+"F4.opExtrude","SWEPT_BODY",BODY,{"disambiguationData":[OSD([sQuery(id+"F0.wireOp",EDGE,"E0")])]}),"instanceName":"14"}),"instanceName":"14"});
            var Q226;
            Q226=makeQuery(id+"F9.opPattern","COPY",BODY,{"derivedFrom":makeQuery(id+"F8.opPattern","COPY",BODY,{"derivedFrom":makeQuery(id+"F4.opExtrude","SWEPT_BODY",BODY,{"disambiguationData":[OSD([sQuery(id+"F0.wireOp",EDGE,"E0")])]}),"instanceName":"15"}),"instanceName":"14"});
            var Q227;
            Q227=makeQuery(id+"F9.opPattern","COPY",BODY,{"derivedFrom":makeQuery(id+"F8.opPattern","COPY",BODY,{"derivedFrom":makeQuery(id+"F4.opExtrude","SWEPT_BODY",BODY,{"disambiguationData":[OSD([sQuery(id+"F0.wireOp",EDGE,"E0")])]}),"instanceName":"6"}),"instanceName":"15"});
            var Q228;
            Q228=makeQuery(id+"F9.opPattern","COPY",BODY,{"derivedFrom":makeQuery(id+"F8.opPattern","COPY",BODY,{"derivedFrom":makeQuery(id+"F4.opExtrude","SWEPT_BODY",BODY,{"disambiguationData":[OSD([sQuery(id+"F0.wireOp",EDGE,"E0")])]}),"instanceName":"7"}),"instanceName":"15"});
            var Q229;
            Q229=makeQuery(id+"F9.opPattern","COPY",BODY,{"derivedFrom":makeQuery(id+"F8.opPattern","COPY",BODY,{"derivedFrom":makeQuery(id+"F4.opExtrude","SWEPT_BODY",BODY,{"disambiguationData":[OSD([sQuery(id+"F0.wireOp",EDGE,"E0")])]}),"instanceName":"13"}),"instanceName":"15"});
            var Q230;
            Q230=makeQuery(id+"F9.opPattern","COPY",BODY,{"derivedFrom":makeQuery(id+"F8.opPattern","COPY",BODY,{"derivedFrom":makeQuery(id+"F4.opExtrude","SWEPT_BODY",BODY,{"disambiguationData":[OSD([sQuery(id+"F0.wireOp",EDGE,"E0")])]}),"instanceName":"14"}),"instanceName":"15"});
            var Q231;
            Q231=makeQuery(id+"F9.opPattern","COPY",BODY,{"derivedFrom":makeQuery(id+"F8.opPattern","COPY",BODY,{"derivedFrom":makeQuery(id+"F4.opExtrude","SWEPT_BODY",BODY,{"disambiguationData":[OSD([sQuery(id+"F0.wireOp",EDGE,"E0")])]}),"instanceName":"15"}),"instanceName":"15"});
            var Q232;
            Q232=makeQuery(id+"F9.opPattern","COPY",BODY,{"derivedFrom":makeQuery(id+"F4.opExtrude","SWEPT_BODY",BODY,{"disambiguationData":[OSD([sQuery(id+"F0.wireOp",EDGE,"E0")])]}),"instanceName":"8"});
            var Q233;
            Q233=makeQuery(id+"F9.opPattern","COPY",BODY,{"derivedFrom":makeQuery(id+"F8.opPattern","COPY",BODY,{"derivedFrom":makeQuery(id+"F4.opExtrude","SWEPT_BODY",BODY,{"disambiguationData":[OSD([sQuery(id+"F0.wireOp",EDGE,"E0")])]}),"instanceName":"12"}),"instanceName":"4"});
            var Q234;
            Q234=makeQuery(id+"F9.opPattern","COPY",BODY,{"derivedFrom":makeQuery(id+"F8.opPattern","COPY",BODY,{"derivedFrom":makeQuery(id+"F4.opExtrude","SWEPT_BODY",BODY,{"disambiguationData":[OSD([sQuery(id+"F0.wireOp",EDGE,"E0")])]}),"instanceName":"8"}),"instanceName":"4"});
            var Q235;
            Q235=makeQuery(id+"F9.opPattern","COPY",BODY,{"derivedFrom":makeQuery(id+"F8.opPattern","COPY",BODY,{"derivedFrom":makeQuery(id+"F4.opExtrude","SWEPT_BODY",BODY,{"disambiguationData":[OSD([sQuery(id+"F0.wireOp",EDGE,"E0")])]}),"instanceName":"4"}),"instanceName":"8"});
            var Q236;
            Q236=makeQuery(id+"F9.opPattern","COPY",BODY,{"derivedFrom":makeQuery(id+"F8.opPattern","COPY",BODY,{"derivedFrom":makeQuery(id+"F4.opExtrude","SWEPT_BODY",BODY,{"disambiguationData":[OSD([sQuery(id+"F0.wireOp",EDGE,"E0")])]}),"instanceName":"8"}),"instanceName":"8"});
            var Q237;
            Q237=makeQuery(id+"F9.opPattern","COPY",BODY,{"derivedFrom":makeQuery(id+"F8.opPattern","COPY",BODY,{"derivedFrom":makeQuery(id+"F4.opExtrude","SWEPT_BODY",BODY,{"disambiguationData":[OSD([sQuery(id+"F0.wireOp",EDGE,"E0")])]}),"instanceName":"12"}),"instanceName":"8"});
            var Q238;
            Q238=makeQuery(id+"F9.opPattern","COPY",BODY,{"derivedFrom":makeQuery(id+"F8.opPattern","COPY",BODY,{"derivedFrom":makeQuery(id+"F4.opExtrude","SWEPT_BODY",BODY,{"disambiguationData":[OSD([sQuery(id+"F0.wireOp",EDGE,"E0")])]}),"instanceName":"4"}),"instanceName":"10"});
            var Q239;
            Q239=makeQuery(id+"F9.opPattern","COPY",BODY,{"derivedFrom":makeQuery(id+"F8.opPattern","COPY",BODY,{"derivedFrom":makeQuery(id+"F4.opExtrude","SWEPT_BODY",BODY,{"disambiguationData":[OSD([sQuery(id+"F0.wireOp",EDGE,"E0")])]}),"instanceName":"8"}),"instanceName":"10"});
            var Q240;
            Q240=makeQuery(id+"F9.opPattern","COPY",BODY,{"derivedFrom":makeQuery(id+"F8.opPattern","COPY",BODY,{"derivedFrom":makeQuery(id+"F4.opExtrude","SWEPT_BODY",BODY,{"disambiguationData":[OSD([sQuery(id+"F0.wireOp",EDGE,"E0")])]}),"instanceName":"12"}),"instanceName":"11"});
            var Q241;
            Q241=makeQuery(id+"F9.opPattern","COPY",BODY,{"derivedFrom":makeQuery(id+"F4.opExtrude","SWEPT_BODY",BODY,{"disambiguationData":[OSD([sQuery(id+"F0.wireOp",EDGE,"E0")])]}),"instanceName":"12"});
            var Q242;
            Q242=makeQuery(id+"F9.opPattern","COPY",BODY,{"derivedFrom":makeQuery(id+"F8.opPattern","COPY",BODY,{"derivedFrom":makeQuery(id+"F4.opExtrude","SWEPT_BODY",BODY,{"disambiguationData":[OSD([sQuery(id+"F0.wireOp",EDGE,"E0")])]}),"instanceName":"12"}),"instanceName":"12"});
            var Q243;
            Q243=makeQuery(id+"F9.opPattern","COPY",BODY,{"derivedFrom":makeQuery(id+"F8.opPattern","COPY",BODY,{"derivedFrom":makeQuery(id+"F4.opExtrude","SWEPT_BODY",BODY,{"disambiguationData":[OSD([sQuery(id+"F0.wireOp",EDGE,"E0")])]}),"instanceName":"14"}),"instanceName":"12"});
            var Q244;
            Q244=makeQuery(id+"F9.opPattern","COPY",BODY,{"derivedFrom":makeQuery(id+"F8.opPattern","COPY",BODY,{"derivedFrom":makeQuery(id+"F4.opExtrude","SWEPT_BODY",BODY,{"disambiguationData":[OSD([sQuery(id+"F0.wireOp",EDGE,"E0")])]}),"instanceName":"8"}),"instanceName":"13"});
            var Q245;
            Q245=makeQuery(id+"F9.opPattern","COPY",BODY,{"derivedFrom":makeQuery(id+"F8.opPattern","COPY",BODY,{"derivedFrom":makeQuery(id+"F4.opExtrude","SWEPT_BODY",BODY,{"disambiguationData":[OSD([sQuery(id+"F0.wireOp",EDGE,"E0")])]}),"instanceName":"12"}),"instanceName":"13"});
            var Q246;
            Q246=makeQuery(id+"F9.opPattern","COPY",BODY,{"derivedFrom":makeQuery(id+"F4.opExtrude","SWEPT_BODY",BODY,{"disambiguationData":[OSD([sQuery(id+"F0.wireOp",EDGE,"E0")])]}),"instanceName":"14"});
            var Q247;
            Q247=makeQuery(id+"F9.opPattern","COPY",BODY,{"derivedFrom":makeQuery(id+"F8.opPattern","COPY",BODY,{"derivedFrom":makeQuery(id+"F4.opExtrude","SWEPT_BODY",BODY,{"disambiguationData":[OSD([sQuery(id+"F0.wireOp",EDGE,"E0")])]}),"instanceName":"4"}),"instanceName":"14"});
            var Q248;
            Q248=makeQuery(id+"F9.opPattern","COPY",BODY,{"derivedFrom":makeQuery(id+"F8.opPattern","COPY",BODY,{"derivedFrom":makeQuery(id+"F4.opExtrude","SWEPT_BODY",BODY,{"disambiguationData":[OSD([sQuery(id+"F0.wireOp",EDGE,"E0")])]}),"instanceName":"8"}),"instanceName":"14"});
            var Q249;
            Q249=makeQuery(id+"F9.opPattern","COPY",BODY,{"derivedFrom":makeQuery(id+"F8.opPattern","COPY",BODY,{"derivedFrom":makeQuery(id+"F4.opExtrude","SWEPT_BODY",BODY,{"disambiguationData":[OSD([sQuery(id+"F0.wireOp",EDGE,"E0")])]}),"instanceName":"12"}),"instanceName":"14"});
            var Q250;
            Q250=makeQuery(id+"F9.opPattern","COPY",BODY,{"derivedFrom":makeQuery(id+"F4.opExtrude","SWEPT_BODY",BODY,{"disambiguationData":[OSD([sQuery(id+"F0.wireOp",EDGE,"E0")])]}),"instanceName":"15"});
            var Q251;
            Q251=makeQuery(id+"F9.opPattern","COPY",BODY,{"derivedFrom":makeQuery(id+"F8.opPattern","COPY",BODY,{"derivedFrom":makeQuery(id+"F4.opExtrude","SWEPT_BODY",BODY,{"disambiguationData":[OSD([sQuery(id+"F0.wireOp",EDGE,"E0")])]}),"instanceName":"4"}),"instanceName":"15"});
            var Q252;
            Q252=makeQuery(id+"F9.opPattern","COPY",BODY,{"derivedFrom":makeQuery(id+"F8.opPattern","COPY",BODY,{"derivedFrom":makeQuery(id+"F4.opExtrude","SWEPT_BODY",BODY,{"disambiguationData":[OSD([sQuery(id+"F0.wireOp",EDGE,"E0")])]}),"instanceName":"8"}),"instanceName":"15"});
            var Q253;
            Q253=makeQuery(id+"F9.opPattern","COPY",BODY,{"derivedFrom":makeQuery(id+"F8.opPattern","COPY",BODY,{"derivedFrom":makeQuery(id+"F4.opExtrude","SWEPT_BODY",BODY,{"disambiguationData":[OSD([sQuery(id+"F0.wireOp",EDGE,"E0")])]}),"instanceName":"4"}),"instanceName":"12"});
            var Q254;
            Q254=makeQuery(id+"F9.opPattern","COPY",BODY,{"derivedFrom":makeQuery(id+"F8.opPattern","COPY",BODY,{"derivedFrom":makeQuery(id+"F4.opExtrude","SWEPT_BODY",BODY,{"disambiguationData":[OSD([sQuery(id+"F0.wireOp",EDGE,"E0")])]}),"instanceName":"8"}),"instanceName":"12"});
            var Q255;
            Q255=makeQuery(id+"F9.opPattern","COPY",BODY,{"derivedFrom":makeQuery(id+"F8.opPattern","COPY",BODY,{"derivedFrom":makeQuery(id+"F4.opExtrude","SWEPT_BODY",BODY,{"disambiguationData":[OSD([sQuery(id+"F0.wireOp",EDGE,"E0")])]}),"instanceName":"12"}),"instanceName":"15"});
            var Q256;
            Q256=sQuery(id+"F2.wireOp",EDGE,"E5");
            circularPattern(context, id + "F9", {"entities" : qUnion([Q0, Q1, Q2, Q3, Q4, Q5, Q6, Q7, Q8, Q9, Q10, Q11, Q12, Q13, Q14, Q15, Q16, Q17, Q18, Q19, Q20, Q21, Q22, Q23, Q24, Q25, Q26, Q27, Q28, Q29, Q30, Q31, Q32, Q33, Q34, Q35, Q36, Q37, Q38, Q39, Q40, Q41, Q42, Q43, Q44, Q45, Q46, Q47, Q48, Q49, Q50, Q51, Q52, Q53, Q54, Q55, Q56, Q57, Q58, Q59, Q60, Q61, Q62, Q63, Q64, Q65, Q66, Q67, Q68, Q69, Q70, Q71, Q72, Q73, Q74, Q75, Q76, Q77, Q78, Q79, Q80, Q81, Q82, Q83, Q84, Q85, Q86, Q87, Q88, Q89, Q90, Q91, Q92, Q93, Q94, Q95, Q96, Q97, Q98, Q99, Q100, Q101, Q102, Q103, Q104, Q105, Q106, Q107, Q108, Q109, Q110, Q111, Q112, Q113, Q114, Q115, Q116, Q117, Q118, Q119, Q120, Q121, Q122, Q123, Q124, Q125, Q126, Q127, Q128, Q129, Q130, Q131, Q132, Q133, Q134, Q135, Q136, Q137, Q138, Q139, Q140, Q141, Q142, Q143, Q144, Q145, Q146, Q147, Q148, Q149, Q150, Q151, Q152, Q153, Q154, Q155, Q156, Q157, Q158, Q159, Q160, Q161, Q162, Q163, Q164, Q165, Q166, Q167, Q168, Q169, Q170, Q171, Q172, Q173, Q174, Q175, Q176, Q177, Q178, Q179, Q180, Q181, Q182, Q183, Q184, Q185, Q186, Q187, Q188, Q189, Q190, Q191, Q192, Q193, Q194, Q195, Q196, Q197, Q198, Q199, Q200, Q201, Q202, Q203, Q204, Q205, Q206, Q207, Q208, Q209, Q210, Q211, Q212, Q213, Q214, Q215, Q216, Q217, Q218, Q219, Q220, Q221, Q222, Q223, Q224, Q225, Q226, Q227, Q228, Q229, Q230, Q231, Q232, Q233, Q234, Q235, Q236, Q237, Q238, Q239, Q240, Q241, Q242, Q243, Q244, Q245, Q246, Q247, Q248, Q249, Q250, Q251, Q252, Q253, Q254, Q255]), "axis" : qUnion([Q256]), "angle" : 360 * degree, "instanceCount" : 16, "equalSpace" : true});
        }
        {
            var Q0;
            Q0=makeQuery(id+"F8.opPattern","COPY",BODY,{"derivedFrom":makeQuery(id+"F4.opExtrude","SWEPT_BODY",BODY,{"disambiguationData":[OSD([sQuery(id+"F0.wireOp",EDGE,"E0")])]}),"instanceName":"4"});
            var Q1;
            Q1=makeQuery(id+"F10.opPattern","COPY",BODY,{"derivedFrom":makeQuery(id+"F8.opPattern","COPY",BODY,{"derivedFrom":makeQuery(id+"F4.opExtrude","SWEPT_BODY",BODY,{"disambiguationData":[OSD([sQuery(id+"F0.wireOp",EDGE,"E0")])]}),"instanceName":"4"}),"instanceName":"3"});
            var Q2;
            Q2=makeQuery(id+"F10.opPattern","COPY",BODY,{"derivedFrom":makeQuery(id+"F8.opPattern","COPY",BODY,{"derivedFrom":makeQuery(id+"F4.opExtrude","SWEPT_BODY",BODY,{"disambiguationData":[OSD([sQuery(id+"F0.wireOp",EDGE,"E0")])]}),"instanceName":"4"}),"instanceName":"2"});
            var Q3;
            Q3=makeQuery(id+"F10.opPattern","COPY",BODY,{"derivedFrom":makeQuery(id+"F8.opPattern","COPY",BODY,{"derivedFrom":makeQuery(id+"F4.opExtrude","SWEPT_BODY",BODY,{"disambiguationData":[OSD([sQuery(id+"F0.wireOp",EDGE,"E0")])]}),"instanceName":"4"}),"instanceName":"1"});
            var Q4;
            Q4=sQuery(id+"F1.wireOp",EDGE,"E3");
            circularPattern(context, id + "F10", {"entities" : qUnion([Q0, Q1, Q2, Q3]), "axis" : qUnion([Q4]), "angle" : 360 * degree, "instanceCount" : 4, "equalSpace" : true});
        }
    });
